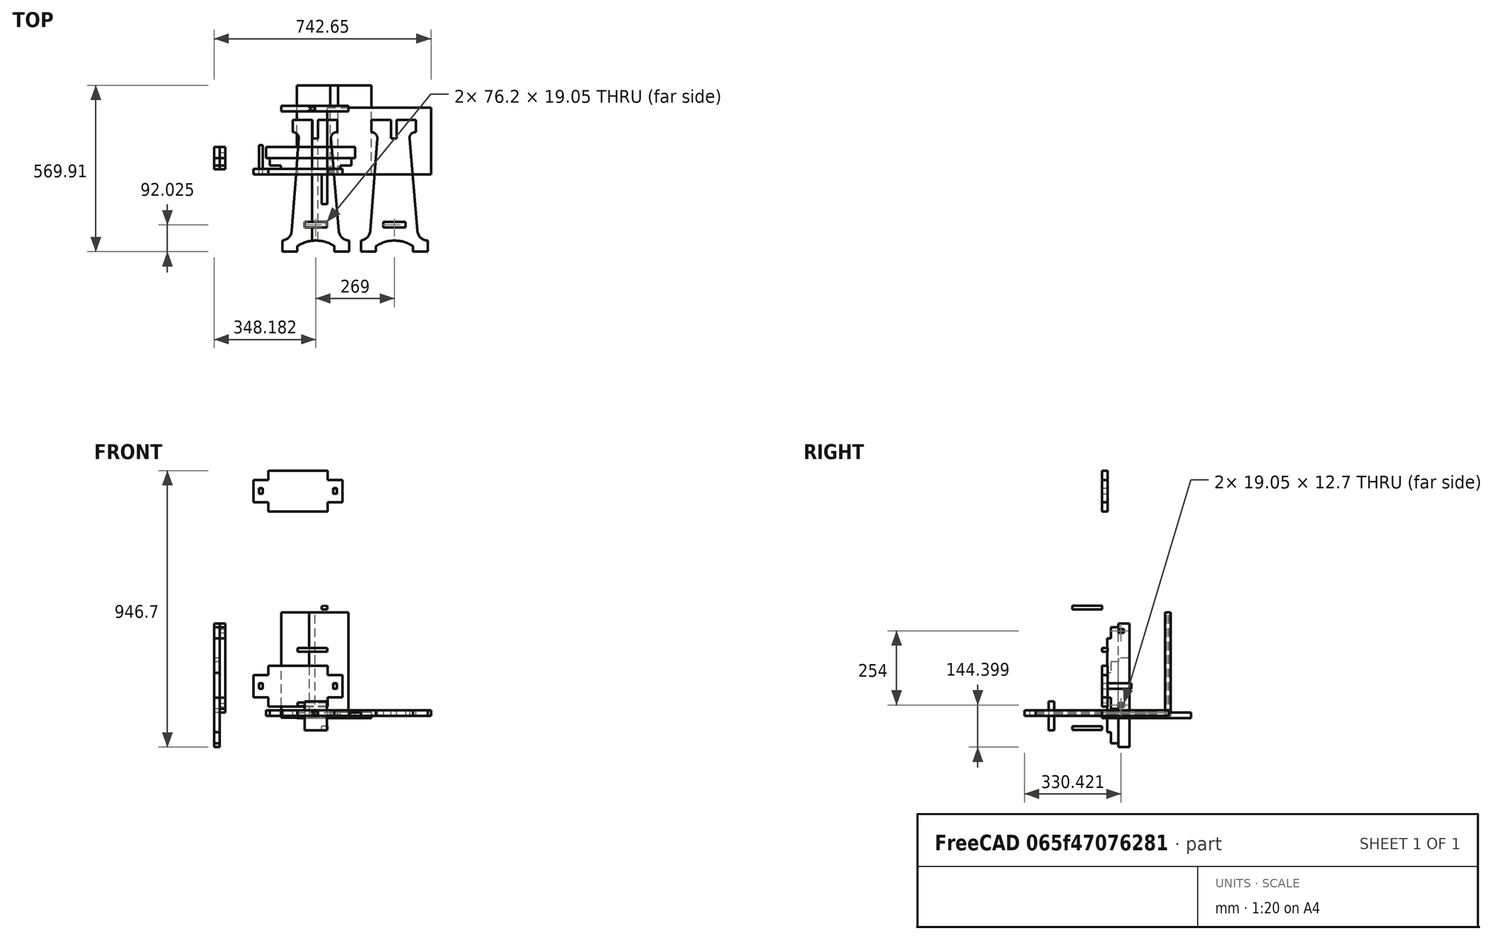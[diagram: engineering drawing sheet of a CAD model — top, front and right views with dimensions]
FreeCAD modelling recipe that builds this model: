
FCSTD DOCUMENT  (FreeCAD 0.20R29177 +426 (Git))
Label: little_table
License: All rights reserved
LicenseURL: http://en.wikipedia.org/wiki/All_rights_reserved
objects: Part::Feature×79, Sketcher::SketchObject×29, Part::Extrusion×28, App::Part×19, Surface::Filling×13, Part::Cut×8, Part::Compound×8, PartDesign::ShapeBinder×5, Part::Wedge×4, Part::Box×4, Part::Part2DObjectPython×4, Surface::GeomFillSurface×4, Part::FeaturePython×3, Part::Face×2, App::FeaturePython×2, App::DocumentObjectGroup×2, Part::MultiFuse×2, Part::Sweep×1, PartDesign::Body×1, Mesh::Feature×1
note: 195 computed .brp shape members not serialized (recipe doc carries the construction recipe); baked Part::Feature solids carry a one-line shape summary decoded from their .brp

FEATURE [Sketcher::SketchObject] Sketch001  label="side"
  FullyConstrained = false
  MapMode = 5
  sketch-geometry (21):
    g0: LineSegment StartX=-117.157 StartY=185.74 StartZ=0 EndX=-50.4825 EndY=185.74 EndZ=0
    g1: LineSegment StartX=-50.4825 StartY=185.74 StartZ=0 EndX=-50.4825 EndY=122.24 EndZ=0
    g2: LineSegment StartX=-50.4825 StartY=122.24 StartZ=0 EndX=-31.4325 EndY=122.24 EndZ=0
    g3: LineSegment StartX=-31.4325 StartY=122.24 StartZ=0 EndX=-31.4325 EndY=185.74 EndZ=0
    g4: LineSegment StartX=-31.4325 StartY=185.74 StartZ=0 EndX=35.2425 EndY=185.74 EndZ=0
    g5: LineSegment StartX=35.2425 StartY=185.74 StartZ=0 EndX=35.2425 EndY=144.465 EndZ=0
    g6: LineSegment StartX=13.0136 StartY=122.055 StartZ=0 EndX=39.774 EndY=-193.522 EndZ=0
    g7: LineSegment StartX=75.3816 StartY=-226.922 StartZ=0 EndX=75.3816 EndY=-265.022 EndZ=0
    g8: LineSegment StartX=75.3816 StartY=-265.022 StartZ=0 EndX=24.5816 EndY=-265.022 EndZ=0
    g9: LineSegment StartX=24.5816 StartY=-265.022 StartZ=0 EndX=24.5816 EndY=-245.972 EndZ=0
    g10: LineSegment StartX=-102.318 StartY=-246.06 StartZ=0 EndX=-102.318 EndY=-265.11 EndZ=0
    g11: LineSegment StartX=-153.118 StartY=-265.11 StartZ=0 EndX=-153.118 EndY=-227.01 EndZ=0
    g12: LineSegment StartX=-121.447 StartY=-193.607 StartZ=0 EndX=-97.2982 EndY=122.181 EndZ=0
    g13: LineSegment StartX=-117.157 StartY=144.465 StartZ=0 EndX=-117.157 EndY=185.74 EndZ=0
    g14: LineSegment StartX=-153.118 StartY=-265.11 StartZ=0 EndX=-102.318 EndY=-265.11 EndZ=0
    g15: ArcOfCircle CenterX=-38.802 CenterY=-341.893 CenterZ=0 NormalX=0 NormalY=0 NormalZ=1 AngleXU=0 Radius=114.971 StartAngle=0.986872 EndAngle=2.15611
    g16: LineSegment StartX=-79.2401 StartY=-226.922 StartZ=0 EndX=17.3359 EndY=-226.922 EndZ=0
    g17: ArcOfCircle CenterX=-157.831 CenterY=-190.825 CenterZ=0 NormalX=0 NormalY=0 NormalZ=1 AngleXU=0 Radius=36.4906 StartAngle=4.8419 EndAngle=6.20686
    g18: ArcOfCircle CenterX=-117.958 CenterY=123.761 CenterZ=0 NormalX=0 NormalY=0 NormalZ=1 AngleXU=0 Radius=20.7201 StartAngle=6.20686 EndAngle=7.81534
    g19: ArcOfCircle CenterX=33.6596 CenterY=123.806 CenterZ=0 NormalX=0 NormalY=0 NormalZ=1 AngleXU=0 Radius=20.7201 StartAngle=1.49433 EndAngle=3.22619
    g20: ArcOfCircle CenterX=76.1341 CenterY=-190.439 CenterZ=0 NormalX=0 NormalY=0 NormalZ=1 AngleXU=0 Radius=36.4906 StartAngle=3.22619 EndAngle=4.69177
  constraints (54):
    c: Coincident(g1,g0)
    c: Vertical(g1)
    c: Coincident(g2,g1)
    c: Coincident(g3,g2)
    c: Coincident(g4,g3)
    c: Horizontal(g4)
    c: Coincident(g5,g4)
    c: Vertical(g5)
    c: Vertical(g7)
    c: Coincident(g8,g7)
    c: Coincident(g9,g8)
    c: Coincident(g13,g0)
    c: Vertical(g13)
    c: Coincident(g14,g10)
    c: Vertical(g3)
    c: Vertical(g11)
    c: Vertical(g10)
    c: Vertical(g9)
    c: Horizontal(g8)
    c: Horizontal(g14)
    c: Horizontal(g0)
    c: Horizontal(g2)
    c: Equal(g4,g0)
    c: Equal(g12,g6)
    c: Equal(g5,g13)
    c: Equal(g11,g7)
    c: Coincident(g11,g14)
    c: Equal(g14,g8)
    c: Equal(g10,g9)
    c: Equal(g3,g1)
    c: DistanceY(g7,g7) = 38.1
    c: DistanceX(g14,g14) = 50.8
    c: DistanceX(g11,g7) = 228.5
    c: DistanceY(g11,g0) = 450.85
    c: DistanceY(g10,g10) = 19.05
    c: DistanceY(g1,g1) = 63.5
    c: DistanceX(g2,g2) = 19.05
    c: DistanceX(g0,g4) = 152.4
    c: DistanceY(g13,g13) = 41.275
    c: Coincident(g15,g9)
    c: Horizontal(g16)
    c: Tangent(g16,g15)
    c: DistanceY(g7,g16) = 38.1
    c: Coincident(g15,g10)
    c: Coincident(g17,g11)
    c: Coincident(g19,g5)
    c: Tangent(g18,g12) = -1.5708
    c: Tangent(g17,g12) = -1.5708
    c: Tangent(g20,g6) = -1.5708
    c: Equal(g19,g18)
    c: Equal(g17,g20)
    c: Coincident(g18,g13)
    c: Tangent(g19,g6) = -1.5708
    c: Coincident(g20,g7)
FEATURE [Part::FeaturePython] Connect  # WARN: FeaturePython — macro-defined, semantics opaque (R4)
  Objects = -> [Sketch001]
  Tolerance = 0
FEATURE [Part::Extrusion] Extrude
  Base = -> Connect
  Dir = (0,0,1)
  DirMode = 2
  FaceMakerClass = Part::FaceMakerBullseye
  LengthFwd = 19.05
  LengthRev = 0
  Solid = true
  Symmetric = false
FEATURE [Part::Extrusion] Extrude001  label="solid_side_leg"
  Base = -> Connect
  Dir = (0,0,1)
  DirMode = 2
  FaceMakerClass = Part::FaceMakerBullseye
  LengthFwd = 19.05
  LengthRev = 0
  Solid = true
  Symmetric = false
FEATURE [Sketcher::SketchObject] Sketch002  label="side_hole"
  ExternalGeometry = -> [Sketch001]
  FullyConstrained = true
  MapMode = 5
  sketch-geometry (4):
    g0: LineSegment StartX=-76.9684 StartY=-163.56 StartZ=0 EndX=-0.768384 EndY=-163.56 EndZ=0
    g1: LineSegment StartX=-0.768384 StartY=-163.56 StartZ=0 EndX=-0.768384 EndY=-182.61 EndZ=0
    g2: LineSegment StartX=-0.768384 StartY=-182.61 StartZ=0 EndX=-76.9684 EndY=-182.61 EndZ=0
    g3: LineSegment StartX=-76.9684 StartY=-182.61 StartZ=0 EndX=-76.9684 EndY=-163.56 EndZ=0
  constraints (12):
    c: Horizontal(g0)
    c: Coincident(g1,g0)
    c: Coincident(g2,g1)
    c: Horizontal(g2)
    c: Vertical(g3)
    c: Coincident(g0,g3)
    c: Coincident(g3,g2)
    c: Vertical(g1)
    c: DistanceX(g0,g0) = 76.2
    c: DistanceY(g3,g3) = 19.05
    c: DistanceY(g-3,g2) = 82.5
    c: DistanceX(g-4,g2) = 76.15
FEATURE [Part::Face] Face
  FaceMakerClass = Part::FaceMakerBullseye
  Sources = -> [Sketch002]
FEATURE [Part::Extrusion] Extrude002  label="rectangular_hole"
  Base = -> Face
  Dir = (0,0,-1)
  DirMode = 0
  FaceMakerClass = Part::FaceMakerBullseye
  LengthFwd = 100
  LengthRev = 0
  Solid = true
  Symmetric = true
FEATURE [PartDesign::ShapeBinder] ShapeBinder
  Support = -> [Extrude001]
  TraceSupport = false
FEATURE [PartDesign::ShapeBinder] ShapeBinder001
  Support = -> [Extrude002]
  TraceSupport = false
FEATURE [Part::Cut] Cut  label="Finished_Side_Leg"
  Base = -> ShapeBinder
  Tool = -> ShapeBinder001
FEATURE [Sketcher::SketchObject] Sketch003  label="hole1"
  FullyConstrained = true
  MapMode = 5
  Placement = pos=(0,0,0) rot=(0.57735,0.57735,0.57735;2.0944rad)
  Support = -> [YZ_Plane007]
FEATURE [Sketcher::SketchObject] Sketch004  label="side001"
  FullyConstrained = false
  MapMode = 5
  Support = -> [XY_Plane006]
  sketch-geometry (21):
    g0: LineSegment StartX=-117.157 StartY=185.74 StartZ=0 EndX=-50.4825 EndY=185.74 EndZ=0
    g1: LineSegment StartX=-50.4825 StartY=185.74 StartZ=0 EndX=-50.4825 EndY=122.24 EndZ=0
    g2: LineSegment StartX=-50.4825 StartY=122.24 StartZ=0 EndX=-31.4325 EndY=122.24 EndZ=0
    g3: LineSegment StartX=-31.4325 StartY=122.24 StartZ=0 EndX=-31.4325 EndY=185.74 EndZ=0
    g4: LineSegment StartX=-31.4325 StartY=185.74 StartZ=0 EndX=35.2425 EndY=185.74 EndZ=0
    g5: LineSegment StartX=35.2425 StartY=185.74 StartZ=0 EndX=35.2425 EndY=144.465 EndZ=0
    g6: LineSegment StartX=13.0136 StartY=122.055 StartZ=0 EndX=39.774 EndY=-193.522 EndZ=0
    g7: LineSegment StartX=75.3816 StartY=-226.922 StartZ=0 EndX=75.3816 EndY=-265.022 EndZ=0
    g8: LineSegment StartX=75.3816 StartY=-265.022 StartZ=0 EndX=24.5816 EndY=-265.022 EndZ=0
    g9: LineSegment StartX=24.5816 StartY=-265.022 StartZ=0 EndX=24.5816 EndY=-245.972 EndZ=0
    g10: LineSegment StartX=-102.318 StartY=-246.06 StartZ=0 EndX=-102.318 EndY=-265.11 EndZ=0
    g11: LineSegment StartX=-153.118 StartY=-265.11 StartZ=0 EndX=-153.118 EndY=-227.01 EndZ=0
    g12: LineSegment StartX=-121.447 StartY=-193.607 StartZ=0 EndX=-97.2982 EndY=122.181 EndZ=0
    g13: LineSegment StartX=-117.157 StartY=144.465 StartZ=0 EndX=-117.157 EndY=185.74 EndZ=0
    g14: LineSegment StartX=-153.118 StartY=-265.11 StartZ=0 EndX=-102.318 EndY=-265.11 EndZ=0
    g15: ArcOfCircle CenterX=-38.802 CenterY=-341.893 CenterZ=0 NormalX=0 NormalY=0 NormalZ=1 AngleXU=0 Radius=114.971 StartAngle=0.986872 EndAngle=2.15611
    g16: LineSegment StartX=-79.2401 StartY=-226.922 StartZ=0 EndX=17.3359 EndY=-226.922 EndZ=0
    g17: ArcOfCircle CenterX=-157.831 CenterY=-190.825 CenterZ=0 NormalX=0 NormalY=0 NormalZ=1 AngleXU=0 Radius=36.4906 StartAngle=4.8419 EndAngle=6.20686
    g18: ArcOfCircle CenterX=-117.958 CenterY=123.761 CenterZ=0 NormalX=0 NormalY=0 NormalZ=1 AngleXU=0 Radius=20.7201 StartAngle=6.20686 EndAngle=7.81534
    g19: ArcOfCircle CenterX=33.6596 CenterY=123.806 CenterZ=0 NormalX=0 NormalY=0 NormalZ=1 AngleXU=0 Radius=20.7201 StartAngle=1.49433 EndAngle=3.22619
    g20: ArcOfCircle CenterX=76.1341 CenterY=-190.439 CenterZ=0 NormalX=0 NormalY=0 NormalZ=1 AngleXU=0 Radius=36.4906 StartAngle=3.22619 EndAngle=4.69177
  constraints (54):
    c: Coincident(g1,g0)
    c: Vertical(g1)
    c: Coincident(g2,g1)
    c: Coincident(g3,g2)
    c: Coincident(g4,g3)
    c: Horizontal(g4)
    c: Coincident(g5,g4)
    c: Vertical(g5)
    c: Vertical(g7)
    c: Coincident(g8,g7)
    c: Coincident(g9,g8)
    c: Coincident(g13,g0)
    c: Vertical(g13)
    c: Coincident(g14,g10)
    c: Vertical(g3)
    c: Vertical(g11)
    c: Vertical(g10)
    c: Vertical(g9)
    c: Horizontal(g8)
    c: Horizontal(g14)
    c: Horizontal(g0)
    c: Horizontal(g2)
    c: Equal(g4,g0)
    c: Equal(g12,g6)
    c: Equal(g5,g13)
    c: Equal(g11,g7)
    c: Coincident(g11,g14)
    c: Equal(g14,g8)
    c: Equal(g10,g9)
    c: Equal(g3,g1)
    c: DistanceY(g7,g7) = 38.1
    c: DistanceX(g14,g14) = 50.8
    c: DistanceX(g11,g7) = 228.5
    c: DistanceY(g11,g0) = 450.85
    c: DistanceY(g10,g10) = 19.05
    c: DistanceY(g1,g1) = 63.5
    c: DistanceX(g2,g2) = 19.05
    c: DistanceX(g0,g4) = 152.4
    c: DistanceY(g13,g13) = 41.275
    c: Coincident(g15,g9)
    c: Horizontal(g16)
    c: Tangent(g16,g15)
    c: DistanceY(g7,g16) = 38.1
    c: Coincident(g15,g10)
    c: Coincident(g17,g11)
    c: Coincident(g19,g5)
    c: Tangent(g18,g12) = -1.5708
    c: Tangent(g17,g12) = -1.5708
    c: Tangent(g20,g6) = -1.5708
    c: Equal(g19,g18)
    c: Equal(g17,g20)
    c: Coincident(g18,g13)
    c: Tangent(g19,g6) = -1.5708
    c: Coincident(g20,g7)
FEATURE [Part::FeaturePython] Connect001  # WARN: FeaturePython — macro-defined, semantics opaque (R4)
  Objects = -> [Sketch004]
  Tolerance = 0
FEATURE [Part::Extrusion] Extrude003
  Base = -> Connect001
  Dir = (0,0,1)
  DirMode = 2
  FaceMakerClass = Part::FaceMakerBullseye
  LengthFwd = 19.05
  LengthRev = 0
  Solid = true
  Symmetric = false
FEATURE [Part::Extrusion] Extrude004  label="solid_side_leg001"
  Base = -> Connect001
  Dir = (0,0,1)
  DirMode = 2
  FaceMakerClass = Part::FaceMakerBullseye
  LengthFwd = 19.05
  LengthRev = 0
  Solid = true
  Symmetric = false
FEATURE [PartDesign::ShapeBinder] ShapeBinder002
  Support = -> [Extrude004]
  TraceSupport = false
FEATURE [Sketcher::SketchObject] Sketch005  label="side_hole001"
  ExternalGeometry = -> [Sketch004]
  FullyConstrained = true
  MapMode = 5
  Support = -> [XY_Plane006]
  sketch-geometry (4):
    g0: LineSegment StartX=-76.9684 StartY=-163.56 StartZ=0 EndX=-0.768384 EndY=-163.56 EndZ=0
    g1: LineSegment StartX=-0.768384 StartY=-163.56 StartZ=0 EndX=-0.768384 EndY=-182.61 EndZ=0
    g2: LineSegment StartX=-0.768384 StartY=-182.61 StartZ=0 EndX=-76.9684 EndY=-182.61 EndZ=0
    g3: LineSegment StartX=-76.9684 StartY=-182.61 StartZ=0 EndX=-76.9684 EndY=-163.56 EndZ=0
  constraints (12):
    c: Horizontal(g0)
    c: Coincident(g1,g0)
    c: Coincident(g2,g1)
    c: Horizontal(g2)
    c: Vertical(g3)
    c: Coincident(g0,g3)
    c: Coincident(g3,g2)
    c: Vertical(g1)
    c: DistanceX(g0,g0) = 76.2
    c: DistanceY(g3,g3) = 19.05
    c: DistanceY(g-3,g2) = 82.5
    c: DistanceX(g-4,g2) = 76.15
FEATURE [Part::Face] Face001
  FaceMakerClass = Part::FaceMakerBullseye
  Sources = -> [Sketch005]
FEATURE [Part::Extrusion] Extrude005  label="rectangular_hole001"
  Base = -> Face001
  Dir = (0,0,-1)
  DirMode = 0
  FaceMakerClass = Part::FaceMakerBullseye
  LengthFwd = 100
  LengthRev = 0
  Solid = true
  Symmetric = true
FEATURE [PartDesign::ShapeBinder] ShapeBinder003
  Support = -> [Extrude005]
  TraceSupport = false
FEATURE [Part::Cut] Cut001  label="Finished_Side_Leg001"
  Base = -> ShapeBinder002
  Placement = pos=(269,0,0) rot=(0,0,1;0rad)
  Tool = -> ShapeBinder003
FEATURE [Sketcher::SketchObject] Sketch006  label="shelf"
  FullyConstrained = false
  MapMode = 5
  Placement = pos=(0,0,0) rot=(1,0,0;1.5708rad)
  Support = -> [XZ_Plane007]
  sketch-geometry (19):
    g0: LineSegment StartX=-202.002 StartY=139.919 StartZ=0 EndX=-202.002 EndY=63.7195 EndZ=0
    g1: LineSegment StartX=-202.002 StartY=63.7195 StartZ=0 EndX=-252.802 EndY=63.7195 EndZ=0
    g2: LineSegment StartX=-252.802 StartY=63.7195 StartZ=0 EndX=-252.802 EndY=139.919 EndZ=0
    g3: LineSegment StartX=-252.802 StartY=139.919 StartZ=0 EndX=-202.002 EndY=139.919 EndZ=0
    g4: LineSegment StartX=-202.002 StartY=139.919 StartZ=0 EndX=-202.002 EndY=171.669 EndZ=0
    g5: LineSegment StartX=-202.002 StartY=63.7195 StartZ=0 EndX=-202.002 EndY=31.9695 EndZ=0
    g6: LineSegment StartX=1.18793 StartY=171.669 StartZ=0 EndX=1.18793 EndY=139.919 EndZ=0
    g7: LineSegment StartX=1.18793 StartY=139.919 StartZ=0 EndX=51.9879 EndY=139.919 EndZ=0
    g8: LineSegment StartX=51.9879 StartY=139.919 StartZ=0 EndX=51.9879 EndY=63.7195 EndZ=0
    g9: LineSegment StartX=51.9879 StartY=63.7195 StartZ=0 EndX=1.18793 EndY=63.7195 EndZ=0
    g10: LineSegment StartX=1.18793 StartY=63.7195 StartZ=0 EndX=1.18793 EndY=31.9695 EndZ=0
    g11: LineSegment StartX=-202.002 StartY=171.669 StartZ=0 EndX=1.18793 EndY=171.669 EndZ=0
    g12: LineSegment StartX=-202.002 StartY=31.9695 StartZ=0 EndX=1.18793 EndY=31.9695 EndZ=0
    g13: LineSegment StartX=1.18793 StartY=139.919 StartZ=0 EndX=1.18793 EndY=63.7195 EndZ=0
    g14: LineSegment StartX=-221.052 StartY=139.919 StartZ=0 EndX=-221.052 EndY=63.7195 EndZ=0
    g15: LineSegment StartX=20.2379 StartY=139.919 StartZ=0 EndX=20.2379 EndY=63.7195 EndZ=0
    g16: LineSegment StartX=20.2379 StartY=63.7195 StartZ=0 EndX=0.408682 EndY=63.7195 EndZ=0
    g17: LineSegment StartX=51.9879 StartY=63.7195 StartZ=0 EndX=20.2379 EndY=63.7195 EndZ=0
    g18: LineSegment StartX=-221.052 StartY=63.7195 StartZ=0 EndX=-252.802 EndY=63.7195 EndZ=0
  constraints (51):
    c: Vertical(g0)
    c: Coincident(g1,g0)
    c: Horizontal(g1)
    c: Coincident(g2,g1)
    c: Vertical(g2)
    c: Coincident(g3,g2)
    c: Coincident(g3,g0)
    c: Horizontal(g3)
    c: Distance(g2) = 76.2
    c: Distance(g3) = 50.8
    c: Perpendicular(g3,g4)
    c: Coincident(g4,g0)
    c: Coincident(g5,g0)
    c: Vertical(g5)
    c: Equal(g5,g4)
    c: Vertical(g6)
    c: Coincident(g7,g6)
    c: Horizontal(g7)
    c: Coincident(g8,g7)
    c: Vertical(g8)
    c: Coincident(g9,g8)
    c: Horizontal(g9)
    c: Coincident(g10,g9)
    c: Vertical(g10)
    c: Distance(g2,g7) = 304.79
    c: Coincident(g11,g4)
    c: Coincident(g11,g6)
    c: Horizontal(g11)
    c: Coincident(g12,g5)
    c: Coincident(g12,g10)
    c: Horizontal(g12)
    c: Equal(g6,g10)
    c: Equal(g10,g5)
    c: Equal(g3,g7)
    c: Equal(g7,g9)
    c: Coincident(g13,g6)
    c: Coincident(g13,g9)
    c: PointOnObject(g14,g3)
    c: PointOnObject(g14,g1)
    c: Vertical(g14)
    c: PointOnObject(g15,g7)
    c: PointOnObject(g15,g9)
    c: Vertical(g15)
    c: Distance(g14,g1) = 31.75
    c: Coincident(g16,g15)
    c: Coincident(g17,g8)
    c: Coincident(g17,g15)
    c: Coincident(g18,g14)
    c: Coincident(g18,g1)
    c: Equal(g17,g18)
    c: Distance(g6,g10) = 139.7
FEATURE [Surface::Filling] Surface
  Anisotropy = false
  BoundaryEdges = -> [Sketch006]
  BoundaryOrder = [0,0,0,0,0,0,0,0,0,0,0,0]
  Degree = 3
  Iterations = 2
  MaximumDegree = 8
  MaximumSegments = 9
  PointsOnCurve = 15
  TolAngular = 0.01
  TolCurvature = 0.1
  Tolerance2d = 1e-05
  Tolerance3d = 0.0001
FEATURE [Part::Extrusion] Extrude006
  Base = -> Surface
  Dir = (0,19.05,0)
  DirMode = 0
  FaceMakerClass = Part::FaceMakerBullseye
  LengthFwd = 19.05
  LengthRev = 0
  Solid = true
  Symmetric = false
FEATURE [Sketcher::SketchObject] Sketch008  label="shelf001"
  FullyConstrained = false
  MapMode = 5
  Placement = pos=(0,0,0) rot=(1,0,0;1.5708rad)
  Support = -> [XZ_Plane008]
  sketch-geometry (19):
    g0: LineSegment StartX=-202.002 StartY=139.919 StartZ=0 EndX=-202.002 EndY=63.7195 EndZ=0
    g1: LineSegment StartX=-202.002 StartY=63.7195 StartZ=0 EndX=-252.802 EndY=63.7195 EndZ=0
    g2: LineSegment StartX=-252.802 StartY=63.7195 StartZ=0 EndX=-252.802 EndY=139.919 EndZ=0
    g3: LineSegment StartX=-252.802 StartY=139.919 StartZ=0 EndX=-202.002 EndY=139.919 EndZ=0
    g4: LineSegment StartX=-202.002 StartY=139.919 StartZ=0 EndX=-202.002 EndY=171.669 EndZ=0
    g5: LineSegment StartX=-202.002 StartY=63.7195 StartZ=0 EndX=-202.002 EndY=31.9695 EndZ=0
    g6: LineSegment StartX=1.18793 StartY=171.669 StartZ=0 EndX=1.18793 EndY=139.919 EndZ=0
    g7: LineSegment StartX=1.18793 StartY=139.919 StartZ=0 EndX=51.9879 EndY=139.919 EndZ=0
    g8: LineSegment StartX=51.9879 StartY=139.919 StartZ=0 EndX=51.9879 EndY=63.7195 EndZ=0
    g9: LineSegment StartX=51.9879 StartY=63.7195 StartZ=0 EndX=1.18793 EndY=63.7195 EndZ=0
    g10: LineSegment StartX=1.18793 StartY=63.7195 StartZ=0 EndX=1.18793 EndY=31.9695 EndZ=0
    g11: LineSegment StartX=-202.002 StartY=171.669 StartZ=0 EndX=1.18793 EndY=171.669 EndZ=0
    g12: LineSegment StartX=-202.002 StartY=31.9695 StartZ=0 EndX=1.18793 EndY=31.9695 EndZ=0
    g13: LineSegment StartX=1.18793 StartY=139.919 StartZ=0 EndX=1.18793 EndY=63.7195 EndZ=0
    g14: LineSegment StartX=-221.052 StartY=139.919 StartZ=0 EndX=-221.052 EndY=63.7195 EndZ=0
    g15: LineSegment StartX=20.2379 StartY=139.919 StartZ=0 EndX=20.2379 EndY=63.7195 EndZ=0
    g16: LineSegment StartX=20.2379 StartY=63.7195 StartZ=0 EndX=0.408682 EndY=63.7195 EndZ=0
    g17: LineSegment StartX=51.9879 StartY=63.7195 StartZ=0 EndX=20.2379 EndY=63.7195 EndZ=0
    g18: LineSegment StartX=-221.052 StartY=63.7195 StartZ=0 EndX=-252.802 EndY=63.7195 EndZ=0
  constraints (51):
    c: Vertical(g0)
    c: Coincident(g1,g0)
    c: Horizontal(g1)
    c: Coincident(g2,g1)
    c: Vertical(g2)
    c: Coincident(g3,g2)
    c: Coincident(g3,g0)
    c: Horizontal(g3)
    c: Distance(g2) = 76.2
    c: Distance(g3) = 50.8
    c: Perpendicular(g3,g4)
    c: Coincident(g4,g0)
    c: Coincident(g5,g0)
    c: Vertical(g5)
    c: Equal(g5,g4)
    c: Vertical(g6)
    c: Coincident(g7,g6)
    c: Horizontal(g7)
    c: Coincident(g8,g7)
    c: Vertical(g8)
    c: Coincident(g9,g8)
    c: Horizontal(g9)
    c: Coincident(g10,g9)
    c: Vertical(g10)
    c: Distance(g2,g7) = 304.79
    c: Coincident(g11,g4)
    c: Coincident(g11,g6)
    c: Horizontal(g11)
    c: Coincident(g12,g5)
    c: Coincident(g12,g10)
    c: Horizontal(g12)
    c: Equal(g6,g10)
    c: Equal(g10,g5)
    c: Equal(g3,g7)
    c: Equal(g7,g9)
    c: Coincident(g13,g6)
    c: Coincident(g13,g9)
    c: PointOnObject(g14,g3)
    c: PointOnObject(g14,g1)
    c: Vertical(g14)
    c: PointOnObject(g15,g7)
    c: PointOnObject(g15,g9)
    c: Vertical(g15)
    c: Distance(g14,g1) = 31.75
    c: Coincident(g16,g15)
    c: Coincident(g17,g8)
    c: Coincident(g17,g15)
    c: Coincident(g18,g14)
    c: Coincident(g18,g1)
    c: Equal(g17,g18)
    c: Distance(g6,g10) = 139.7
FEATURE [Sketcher::SketchObject] Sketch009
  ExternalGeometry = -> [Sketch008]
  FullyConstrained = true
  Placement = pos=(0,0,0) rot=(1,0,0;1.5708rad)
  sketch-geometry (4):
    g0: LineSegment StartX=-221.052 StartY=111.344 StartZ=0 EndX=-233.752 EndY=111.344 EndZ=0
    g1: LineSegment StartX=-233.752 StartY=111.344 StartZ=0 EndX=-233.752 EndY=92.2945 EndZ=0
    g2: LineSegment StartX=-233.752 StartY=92.2945 StartZ=0 EndX=-221.052 EndY=92.2945 EndZ=0
    g3: LineSegment StartX=-221.052 StartY=92.2945 StartZ=0 EndX=-221.052 EndY=111.344 EndZ=0
  constraints (12):
    c: Coincident(g0,g1)
    c: Coincident(g1,g2)
    c: Coincident(g2,g3)
    c: Coincident(g3,g0)
    c: Horizontal(g0)
    c: Horizontal(g2)
    c: Vertical(g1)
    c: Vertical(g3)
    c: Distance(g3) = 19.05
    c: Distance(g0) = 12.7
    c: PointOnObject(g0,g-3)
    c: Distance(g0,g-3) = 28.575
FEATURE [Sketcher::SketchObject] Sketch010
  ExternalGeometry = -> [Sketch006]
  FullyConstrained = true
  MapMode = 2
  Placement = pos=(0,0,0) rot=(1,0,0;1.5708rad)
  Support = -> [Sketch006]
  sketch-geometry (4):
    g0: LineSegment StartX=20.2379 StartY=111.344 StartZ=0 EndX=32.9379 EndY=111.344 EndZ=0
    g1: LineSegment StartX=32.9379 StartY=111.344 StartZ=0 EndX=32.9379 EndY=92.2945 EndZ=0
    g2: LineSegment StartX=32.9379 StartY=92.2945 StartZ=0 EndX=20.2379 EndY=92.2945 EndZ=0
    g3: LineSegment StartX=20.2379 StartY=92.2945 StartZ=0 EndX=20.2379 EndY=111.344 EndZ=0
  constraints (12):
    c: Coincident(g0,g1)
    c: Coincident(g1,g2)
    c: Coincident(g2,g3)
    c: Coincident(g3,g0)
    c: Horizontal(g0)
    c: Horizontal(g2)
    c: Vertical(g1)
    c: Vertical(g3)
    c: Distance(g1) = 19.05
    c: Distance(g0) = 12.7
    c: PointOnObject(g0,g-3)
    c: Distance(g0,g-3) = 28.575
FEATURE [Surface::Filling] Surface007  label="hole2"
  Anisotropy = false
  BoundaryEdges = -> [Sketch010]
  BoundaryOrder = [0,0,0,0]
  Degree = 3
  Iterations = 2
  MaximumDegree = 8
  MaximumSegments = 9
  PointsOnCurve = 15
  TolAngular = 0.01
  TolCurvature = 0.1
  Tolerance2d = 1e-05
  Tolerance3d = 0.0001
FEATURE [Surface::Filling] Surface008  label="hole003"
  Anisotropy = false
  BoundaryEdges = -> [Sketch009]
  BoundaryOrder = [0,0,0,0]
  Degree = 3
  Iterations = 2
  MaximumDegree = 8
  MaximumSegments = 9
  PointsOnCurve = 15
  TolAngular = 0.01
  TolCurvature = 0.1
  Tolerance2d = 1e-05
  Tolerance3d = 0.0001
FEATURE [Part::Extrusion] Extrude007
  Base = -> Surface008
  Dir = (0,200,0)
  DirMode = 0
  FaceMakerClass = Part::FaceMakerBullseye
  LengthFwd = 100
  LengthRev = 0
  Solid = true
  Symmetric = false
FEATURE [Part::Extrusion] Extrude008
  Base = -> Surface008
  Dir = (0,100,0)
  DirMode = 0
  FaceMakerClass = Part::FaceMakerBullseye
  LengthFwd = 100
  LengthRev = 0
  Solid = true
  Symmetric = false
FEATURE [Part::Cut] Cut002
  Base = -> Extrude006
  Tool = -> Extrude007
FEATURE [Part::Extrusion] Extrude009
  Base = -> Surface007
  Dir = (0,100,-1)
  DirMode = 0
  FaceMakerClass = Part::FaceMakerBullseye
  LengthFwd = 100
  LengthRev = 0
  Solid = false
  Symmetric = false
FEATURE [Part::Cut] Cut003
  Base = -> Cut002
  Tool = -> Extrude009
FEATURE [Sketcher::SketchObject] Sketch011
  FullyConstrained = false
  MapMode = 5
  Placement = pos=(0,0,0) rot=(0.57735,0.57735,0.57735;2.0944rad)
  Support = -> [YZ_Plane014]
  sketch-geometry (4):
    g0: LineSegment StartX=-13 StartY=37.953 StartZ=0 EndX=0 EndY=37.953 EndZ=0
    g1: LineSegment StartX=0 StartY=37.953 StartZ=0 EndX=0 EndY=18.903 EndZ=0
    g2: LineSegment StartX=0 StartY=18.903 StartZ=0 EndX=-13 EndY=18.903 EndZ=0
    g3: LineSegment StartX=-13 StartY=18.903 StartZ=0 EndX=-13 EndY=37.953 EndZ=0
  constraints (11):
    c: Coincident(g0,g1)
    c: Coincident(g1,g2)
    c: Coincident(g2,g3)
    c: Coincident(g3,g0)
    c: Horizontal(g0)
    c: Horizontal(g2)
    c: Vertical(g1)
    c: Vertical(g3)
    c: PointOnObject(g1,g-2)
    c: Distance(g0) = 13
    c: Distance(g1) = 19.05
FEATURE [App::Part] Part007
  Origin = -> Origin009
FEATURE [App::Part] Part
  Group = -> [Part007]
  Origin = -> Origin008
FEATURE [Part::Wedge] Wedge
  AttacherType = Attacher::AttachEngine3D
  Placement = pos=(0,4.4e-14,364) rot=(0.57735,-0.57735,0.57735;2.0944rad)
  X2max = 12
  X2min = 0
  Xmax = 13
  Xmin = 0
  Ymax = 19.05
  Ymin = 0
  Z2max = 101.6
  Z2min = 0
  Zmax = 101.6
  Zmin = 0
FEATURE [Part::Wedge] Wedge001
  AttacherType = Attacher::AttachEngine3D
  Placement = pos=(0,4.4e-14,-48) rot=(0.57735,-0.57735,0.57735;2.0944rad)
  X2max = 12
  X2min = 0
  Xmax = 13
  Xmin = 0
  Ymax = 19.05
  Ymin = 0
  Z2max = 101.6
  Z2min = 0
  Zmax = 101.6
  Zmin = 0
FEATURE [Part::Wedge] Wedge002
  AttacherType = Attacher::AttachEngine3D
  Placement = pos=(-1.6e-14,4.4e-14,220) rot=(0,-1,0;1.5708rad)
  X2max = 12
  X2min = 0
  Xmax = 13
  Xmin = 0
  Ymax = 19.05
  Ymin = 0
  Z2max = 101.6
  Z2min = 0
  Zmax = 101.6
  Zmin = 0
FEATURE [Part::Wedge] Wedge003
  AttacherType = Attacher::AttachEngine3D
  Placement = pos=(-1.8e-14,4.4e-14,33) rot=(0,-1,0;1.5708rad)
  X2max = 12
  X2min = 0
  Xmax = 13
  Xmin = 0
  Ymax = 19.05
  Ymin = 0
  Z2max = 101.6
  Z2min = 0
  Zmax = 101.6
  Zmin = 0
FEATURE [App::Part] Part008  label="wedge"
  Group = -> [Wedge,Wedge001,Wedge002,Wedge003]
  Origin = -> Origin010
FEATURE [Part::Box] Box
  AttacherType = Attacher::AttachEngine3D
  Height = 19
  Length = 360
  Placement = pos=(-157,216,-6) rot=(0.57735,0.57735,0.57735;4.18879rad)
  Width = 230
FEATURE [Sketcher::SketchObject] Sketch013
  FullyConstrained = false
  MapMode = 2
  sketch-geometry (17):
    g0: LineSegment StartX=-121.471 StartY=102.917 StartZ=0 EndX=183.329 EndY=102.917 EndZ=0
    g1: ArcOfCircle CenterX=26.5868 CenterY=-67.4245 CenterZ=0 NormalX=0 NormalY=0 NormalZ=1 AngleXU=0 Radius=83.7769 StartAngle=1.18434 EndAngle=2.04007
    g2: LineSegment StartX=58.1627 StartY=10.1739 StartZ=0 EndX=110.81 EndY=10.1739 EndZ=0
    g3: LineSegment StartX=110.81 StartY=36.9335 StartZ=0 EndX=110.81 EndY=10.1739 EndZ=0
    g4: LineSegment StartX=-11.3006 StartY=7.29566 StartZ=0 EndX=-63.9482 EndY=7.29566 EndZ=0
    g5: LineSegment StartX=-63.9482 StartY=7.29566 StartZ=0 EndX=-63.9482 EndY=34.0552 EndZ=0
    g6: LineSegment StartX=-99.4978 StartY=42.1194 StartZ=0 EndX=-63.9482 EndY=34.0552 EndZ=0
    g7: LineSegment StartX=147.263 StartY=36.9335 StartZ=0 EndX=110.81 EndY=36.9335 EndZ=0
    g8: ArcOfCircle CenterX=-121.241 CenterY=53.2491 CenterZ=0 NormalX=0 NormalY=0 NormalZ=1 AngleXU=0 Radius=21.7431 StartAngle=3e-16 EndAngle=0.865607
    g9: LineSegment StartX=183.329 StartY=102.917 StartZ=0 EndX=183.329 EndY=69.8062 EndZ=0
    g10: LineSegment StartX=-121.471 StartY=102.917 StartZ=0 EndX=-121.471 EndY=69.8062 EndZ=0
    g11: LineSegment StartX=147.263 StartY=48.0632 StartZ=0 EndX=147.263 EndY=36.9335 EndZ=0
    g12: LineSegment StartX=-99.4978 StartY=53.2491 StartZ=0 EndX=-99.4978 EndY=42.1194 EndZ=0
    g13: LineSegment StartX=169.006 StartY=69.8062 StartZ=0 EndX=183.329 EndY=69.8062 EndZ=0
    g14: LineSegment StartX=-107.148 StartY=69.8062 StartZ=0 EndX=-121.471 EndY=69.8062 EndZ=0
    g15: LineSegment StartX=-107.148 StartY=69.8062 StartZ=0 EndX=169.006 EndY=69.8062 EndZ=0
    g16: ArcOfCircle CenterX=169.006 CenterY=48.0632 CenterZ=0 NormalX=0 NormalY=0 NormalZ=1 AngleXU=0 Radius=21.7431 StartAngle=1.5708 EndAngle=3.14159
  constraints (40):
    c: Horizontal(g0)
    c: Distance(g0) = 304.8
    c: Horizontal(g4)
    c: Horizontal(g7)
    c: Equal(g5,g3)
    c: Equal(g4,g2)
    c: Perpendicular(g3,g2)
    c: Coincident(g15,g8)
    c: Horizontal(g15)
    c: Coincident(g10,g14)
    c: Coincident(g9,g0)
    c: Coincident(g9,g13)
    c: Perpendicular(g0,g9)
    c: Coincident(g0,g10)
    c: Equal(g14,g13)
    c: Perpendicular(g0,g10)
    c: Coincident(g8,g14)
    c: Equal(g9,g10)
    c: Tangent(g16,g13) = 1.5708
    c: Perpendicular(g9,g13)
    c: Tangent(g16,g11) = -1.5708
    c: Coincident(g15,g13)
    c: Tangent(g8,g12) = 1.5708
    c: Coincident(g6,g12)
    c: Equal(g6,g7)
    c: Perpendicular(g0,g5)
    c: Coincident(g8,g12)
    c: Coincident(g4,g1)
    c: Coincident(g4,g5)
    c: Coincident(g16,g11)
    c: Coincident(g11,g7)
    c: Perpendicular(g0,g12)
    c: Coincident(g2,g1)
    c: Coincident(g3,g2)
    c: Coincident(g7,g3)
    c: Perpendicular(g7,g3)
    c: Equal(g16,g8)
    c: Equal(g12,g11)
    c: Perpendicular(g7,g11)
    c: Coincident(g6,g5)
FEATURE [App::FeaturePython] logo  # WARN: FeaturePython — macro-defined, semantics opaque (R4)
  BaseHeight = 0.5
  LayerHeight = 0.1
  MaximumHeight = 3
  NozzleSize = 0.4
  Path = <userpath>/Documents/glas/website/logo.png
  UpdateNotifier = 6
  ppi = 300
FEATURE [Part::Feature] Extrude010_solid  label="Extrude010 (Solid)"
  Placement = pos=(0,0,119) rot=(0,0,1;0rad)
  shape: bbox 19.05 x 80.33 x 335.3 mm, 17 faces (baked)
FEATURE [Part::FeaturePython] CrossPiece  # WARN: FeaturePython — macro-defined, semantics opaque (R4)
FEATURE [Sketcher::SketchObject] Sketch016
  ExternalGeometry = -> [Box]
  FullyConstrained = true
  MapMode = 5
  Placement = pos=(-157,216,354) rot=(0,0,1;0rad)
  Support = -> [Box]
  sketch-geometry (3):
    g0: LineSegment StartX=115 StartY=19 StartZ=0 EndX=115 EndY=0 EndZ=0
    g1: LineSegment StartX=115 StartY=19 StartZ=0 EndX=230 EndY=19 EndZ=0
    g2: LineSegment StartX=115 StartY=19 StartZ=0 EndX=0 EndY=19 EndZ=0
  constraints (8):
    c: PointOnObject(g0,g-5)
    c: PointOnObject(g0,g-6)
    c: Vertical(g0)
    c: Coincident(g1,g0)
    c: Coincident(g1,g-5)
    c: Coincident(g2,g0)
    c: Coincident(g2,g-5)
    c: Equal(g1,g2)
FEATURE [Part::Feature] Box_cs
  shape: bbox 3e-07 x 19 x 360 mm, 0 faces, 0 solids (baked)
FEATURE [Part::Feature] Box_cs001
  shape: bbox 3e-07 x 19 x 360 mm, 0 faces, 0 solids (baked)
FEATURE [Surface::Filling] Surface006
  Anisotropy = false
  Degree = 3
  Iterations = 2
  MaximumDegree = 8
  MaximumSegments = 9
  PointsOnCurve = 15
  TolAngular = 0.01
  TolCurvature = 0.1
  Tolerance2d = 1e-05
  Tolerance3d = 0.0001
FEATURE [Surface::Filling] Surface005
  Anisotropy = false
  BoundaryEdges = -> [Sketch006]
  BoundaryOrder = [0]
  Degree = 3
  Iterations = 2
  MaximumDegree = 8
  MaximumSegments = 9
  PointsOnCurve = 15
  TolAngular = 0.01
  TolCurvature = 0.1
  Tolerance2d = 1e-05
  Tolerance3d = 0.0001
FEATURE [Surface::Filling] Surface004
  Anisotropy = false
  BoundaryEdges = -> [Sketch010]
  Degree = 3
  Iterations = 2
  MaximumDegree = 8
  MaximumSegments = 9
  PointsOnCurve = 15
  TolAngular = 0.01
  TolCurvature = 0.1
  Tolerance2d = 1e-05
  Tolerance3d = 0.0001
FEATURE [Part::Part2DObjectPython] Line  label="Line_Master_Line"  # Draft 2D object (typed FeaturePython)
  Area = 0
  ChamferSize = 0
  Closed = false
  End = (-42,225.5,174)
  FilletRadius = 0
  Length = 0
  MakeFace = false
  Points = (2) [(-42,225.5,174),(-42,225.5,174)]
  Start = (-42,225.5,174)
  Subdivisions = 0
FEATURE [Part::Part2DObjectPython] Polygon  label="Forme_Polygon"  # Draft 2D object (typed FeaturePython)
  Area = 0
  ChamferSize = 0
  DrawMode = 1
  FacesNumber = 3
  FilletRadius = 0
  MakeFace = false
  Placement = pos=(-42,225.5,174) rot=(0,1,0;2.67794rad)
  Radius = 5
FEATURE [Part::Sweep] Sweep_Externe_
  Frenet = true
  Sections = -> [Polygon]
  Solid = true
  Spine = -> Line
  Transition = 1
FEATURE [App::Part] Part010  label="top"
  Group = -> [Box_cs,Polygon,Sweep_Externe_,Line]
  Origin = -> Origin012
FEATURE [App::Part] Part012  label="top001"
  Group = -> [Part010,Box,Sketch016,Box_cs001,Part,Sketch011]
  Origin = -> Origin014
FEATURE [Sketcher::SketchObject] Sketch017
  FullyConstrained = false
  MapMode = 5
  Placement = pos=(0,0,0) rot=(1,0,0;1.5708rad)
  Support = -> [XZ_Plane016]
  sketch-geometry (4):
    g0: LineSegment StartX=-103.59 StartY=11.0494 StartZ=0 EndX=36.7099 EndY=11.0494 EndZ=0
    g1: LineSegment StartX=36.7099 StartY=11.0494 StartZ=0 EndX=36.7099 EndY=-8.00061 EndZ=0
    g2: LineSegment StartX=36.7099 StartY=-8.00061 StartZ=0 EndX=-103.59 EndY=-8.00061 EndZ=0
    g3: LineSegment StartX=-103.59 StartY=-8.00061 StartZ=0 EndX=-103.59 EndY=11.0494 EndZ=0
  constraints (10):
    c: Coincident(g0,g1)
    c: Coincident(g1,g2)
    c: Coincident(g2,g3)
    c: Coincident(g3,g0)
    c: Horizontal(g0)
    c: Horizontal(g2)
    c: Vertical(g1)
    c: Vertical(g3)
    c: Distance(g3) = 19.05
    c: Distance(g0) = 140.3
FEATURE [Sketcher::SketchObject] Sketch018
  ExternalGeometry = -> [Sketch017]
  FullyConstrained = true
  MapMode = 5
  Placement = pos=(0,0,0) rot=(1,0,0;1.5708rad)
  Support = -> [XZ_Plane016]
  sketch-geometry (4):
    g0: LineSegment StartX=151.01 StartY=11.0494 StartZ=0 EndX=10.7099 EndY=11.0494 EndZ=0
    g1: LineSegment StartX=10.7099 StartY=11.0494 StartZ=0 EndX=10.7099 EndY=-8.00061 EndZ=0
    g2: LineSegment StartX=10.7099 StartY=-8.00061 StartZ=0 EndX=151.01 EndY=-8.00061 EndZ=0
    g3: LineSegment StartX=151.01 StartY=-8.00061 StartZ=0 EndX=151.01 EndY=11.0494 EndZ=0
  constraints (11):
    c: Coincident(g0,g1)
    c: Coincident(g1,g2)
    c: Coincident(g2,g3)
    c: Coincident(g3,g0)
    c: Horizontal(g2)
    c: Vertical(g1)
    c: Vertical(g3)
    c: Equal(g-5,g1)
    c: Equal(g0,g-3)
    c: Tangent(g0,g-3)
    c: Distance(g-5,g0) = 26
FEATURE [Surface::GeomFillSurface] Surface012
  BoundaryList = -> [Sketch017]
  FillType = 0
FEATURE [Surface::GeomFillSurface] Surface013
  BoundaryList = -> [Sketch018]
  FillType = 0
FEATURE [Part::Extrusion] Extrude012
  Base = -> Surface012
  Dir = (0,1,0)
  DirMode = 0
  FaceMakerClass = Part::FaceMakerBullseye
  LengthFwd = 304.8
  LengthRev = 0
  Solid = true
  Symmetric = false
FEATURE [Part::Extrusion] Extrude013
  Base = -> Surface013
  Dir = (0,1,0)
  DirMode = 0
  FaceMakerClass = Part::FaceMakerBullseye
  LengthFwd = 304.8
  LengthRev = 0
  Solid = false
  Symmetric = false
FEATURE [App::Part] Part013
  Group = -> [Sketch017,Sketch018,Surface012,Surface013,Extrude012,Extrude013]
  Origin = -> Origin015
FEATURE [Part::Box] Box001
  AttacherType = Attacher::AttachEngine3D
  Height = 19.05
  Length = 355.6
  Width = 228.6
FEATURE [Sketcher::SketchObject] Sketch019
  FullyConstrained = false
  MapMode = 4
  Placement = pos=(0,0,0) rot=(0.57735,0.57735,0.57735;2.0944rad)
  Support = -> [Box001]
  sketch-geometry (9):
    g0: LineSegment StartX=94.1694 StartY=63.8544 StartZ=0 EndX=94.1694 EndY=47.0374 EndZ=0
    g1: LineSegment StartX=94.1694 StartY=47.0374 StartZ=0 EndX=110.986 EndY=49.1934 EndZ=0
    g2: LineSegment StartX=110.986 StartY=49.1934 StartZ=0 EndX=110.986 EndY=39.4913 EndZ=0
    g3: LineSegment StartX=110.986 StartY=39.4913 StartZ=0 EndX=94.1694 EndY=40.5691 EndZ=0
    g4: LineSegment StartX=94.1694 StartY=40.5691 StartZ=0 EndX=94.1694 EndY=27.6332 EndZ=0
    g5: LineSegment StartX=94.1694 StartY=53.8237 StartZ=0 EndX=120.169 EndY=53.8237 EndZ=0
    g6: LineSegment StartX=120.169 StartY=53.8237 StartZ=0 EndX=120.169 EndY=34.7737 EndZ=0
    g7: LineSegment StartX=120.169 StartY=34.7737 StartZ=0 EndX=94.1694 EndY=34.7737 EndZ=0
    g8: LineSegment StartX=94.1694 StartY=34.7737 StartZ=0 EndX=94.1694 EndY=53.8237 EndZ=0
  constraints (17):
    c: Vertical(g0)
    c: Coincident(g1,g0)
    c: Coincident(g2,g1)
    c: Vertical(g2)
    c: Coincident(g3,g2)
    c: Coincident(g4,g3)
    c: Coincident(g5,g6)
    c: Coincident(g6,g7)
    c: Coincident(g7,g8)
    c: Coincident(g8,g5)
    c: Horizontal(g5)
    c: Horizontal(g7)
    c: Vertical(g6)
    c: DistanceX(g5,g5) = 26
    c: DistanceY(g8,g8) = 19.05
    c: Tangent(g4,g8)
    c: Tangent(g0,g8)
FEATURE [App::Part] Part014  label="good"
  Group = -> [Box001,Sketch019]
  Origin = -> Origin016
FEATURE [Part::Box] Box002
  AttacherType = Attacher::AttachEngine3D
  Height = 19.05
  Length = 355.6
  Width = 228.6
FEATURE [Sketcher::SketchObject] Sketch020
  ExternalGeometry = -> [Box002]
  FullyConstrained = false
  MapMode = 4
  Placement = pos=(0,0,0) rot=(0.57735,0.57735,0.57735;2.0944rad)
  Support = -> [Box002]
  sketch-geometry (1):
    g0: LineSegment StartX=114.3 StartY=19.05 StartZ=0 EndX=114.3 EndY=0.241736 EndZ=0
  constraints (3):
    c: PointOnObject(g0,g-3)
    c: Perpendicular(g-3,g0)
    c: Distance(g0,g-3) = 114.3
FEATURE [App::Part] Part015  label="good001"
  Group = -> [Box002,Sketch020]
  Origin = -> Origin017
FEATURE [App::DocumentObjectGroup] Group  label="top work"
  Group = -> [Part012,Part013,Part014,Part015]
FEATURE [Part::Feature] Face002 .. Face005  x4 (patterned run collapsed; names and placements below)
  shape: bbox 115 x 19 x 3e-07 mm, 1 faces, 0 solids (baked)
FEATURE [Part::Feature] Face006
  Placement = pos=(-157,216,-6) rot=(0.57735,0.57735,0.57735;4.18879rad)
  shape: bbox 2e-07 x 19 x 360 mm, 1 faces, 0 solids (baked)
FEATURE [Part::Feature] Face007
  Placement = pos=(-157,216,-6) rot=(0.57735,0.57735,0.57735;4.18879rad)
  shape: bbox 2e-07 x 19 x 360 mm, 1 faces, 0 solids (baked)
FEATURE [Part::Feature] Face008 .. Face011  x4 (patterned run collapsed; names and placements below)
  shape: bbox 115 x 3e-07 x 360 mm, 1 faces, 0 solids (baked)
FEATURE [Part::Feature] Box_cs002
  shape: bbox 3e-07 x 19 x 360 mm, 0 faces, 0 solids (baked)
FEATURE [Part::Feature] Box_cs003
  shape: bbox 3e-07 x 19 x 360 mm, 0 faces, 0 solids (baked)
FEATURE [Part::Compound] Compound
  Links = -> [Face003,Face005,Face009,Face007,Face011,Box_cs002]
FEATURE [Part::Feature] Compound_solid  label="Compound (Solid)"
  Placement = pos=(0,-161,0) rot=(0,0,1;0rad)
  shape: bbox 115 x 19 x 360 mm, 5 faces (baked)
FEATURE [Part::Compound] Compound001
  Links = -> [Face002,Face004,Face006,Face008,Face010,Box_cs003]
FEATURE [Part::Feature] Compound001_solid  label="Compound001 (Solid)"
  Placement = pos=(0,-308,0) rot=(0,0,1;0rad)
  shape: bbox 115 x 19 x 360 mm, 5 faces (baked)
FEATURE [Part::Compound] Compound002
  Links = -> [Extrude010_solid]
FEATURE [Surface::GeomFillSurface] Surface014
  BoundaryList = -> [Compound001_solid]
  FillType = 0
FEATURE [Surface::GeomFillSurface] Surface015
  BoundaryList = -> [Compound_solid]
  FillType = 0
FEATURE [Part::Compound] Compound003
  Links = -> [Compound_solid,Surface015]
FEATURE [App::Part] Part017
  Group = -> [Face003,Face005,Face007,Face009,Face011,Box_cs002,Compound,Compound_solid,Surface015,Compound003]
  Origin = -> Origin019
  Placement = pos=(0,-147,0) rot=(0,0,1;0rad)
FEATURE [Part::Compound] Compound004
  Links = -> [Surface014,Compound001_solid]
FEATURE [Part::Feature] Compound004_solid  label="Compound004 (Solid)"
  shape: bbox 115 x 19 x 360 mm, 6 faces (baked)
FEATURE [App::Part] Part016  label="piece1"
  Group = -> [Face002,Face004,Face006,Face008,Face010,Box_cs003,Compound001,Compound001_solid,Surface014,Compound004,Compound004_solid]
  Origin = -> Origin018
FEATURE [Part::Box] Box003
  AttacherType = Attacher::AttachEngine3D
  Height = 19
  Length = 360
  Placement = pos=(-157,216,-6) rot=(0.57735,0.57735,0.57735;4.18879rad)
  Width = 230
FEATURE [PartDesign::ShapeBinder] ShapeBinder004
  TraceSupport = false
FEATURE [PartDesign::Body] Body
  Origin = -> Origin
FEATURE [Part::Feature] Wire
  shape: bbox 19.05 x 19.05 x 2e-07 mm, 0 faces, 0 solids (baked)
FEATURE [Part::Feature] Wire001
  Placement = pos=(-244,89,-184) rot=(0,0,-1;1.5708rad)
  shape: bbox 19.69 x 59.95 x 2e-07 mm, 0 faces, 0 solids (baked)
FEATURE [Part::Extrusion] Extrude014
  Base = -> Wire001
  Dir = (0,0,1)
  DirMode = 2
  FaceMakerClass = Part::FaceMakerBullseye
  LengthFwd = 500
  LengthRev = 0
  Placement = pos=(0,77,56) rot=(0,0,1;0rad)
  Solid = false
  Symmetric = false
FEATURE [Part::Feature] Solid  label="penis"
  shape: bbox 115.3 x 19 x 360 mm, 11 faces (baked)
FEATURE [Part::Feature] Solid001  label="vagina"
  shape: bbox 134.4 x 19 x 360 mm, 11 faces (baked)
FEATURE [App::Part] Part018  label="final top"
  Group = -> [Box003,Wire,Wire001,Extrude014,ShapeBinder004,Solid001,Solid]
  Origin = -> Origin020
FEATURE [Part::Feature] Wire002
  Placement = pos=(-244,89,-184) rot=(0,0,-1;1.5708rad)
  shape: bbox 19.69 x 59.95 x 2e-07 mm, 0 faces, 0 solids (baked)
FEATURE [Part::Extrusion] Extrude015
  Base = -> Wire002
  Dir = (0,0,1)
  DirMode = 2
  FaceMakerClass = Part::FaceMakerBullseye
  LengthFwd = 500
  LengthRev = 0
  Placement = pos=(10,-85,157) rot=(-1,0,0;1.5708rad)
  Solid = false
  Symmetric = false
FEATURE [Part::Feature] Wire003
  Placement = pos=(-244,89,-184) rot=(0,0,-1;1.5708rad)
  shape: bbox 19.69 x 59.95 x 2e-07 mm, 0 faces, 0 solids (baked)
FEATURE [Part::Extrusion] Extrude016
  Base = -> Wire003
  Dir = (0,0,1)
  DirMode = 2
  FaceMakerClass = Part::FaceMakerBullseye
  LengthFwd = 500
  LengthRev = 0
  Placement = pos=(10,46.9287,-138.48) rot=(1,0,0;1.5708rad)
  Solid = false
  Symmetric = false
FEATURE [Part::Feature] Solid002  label="penis001"
  shape: bbox 121.4 x 450.9 x 19.05 mm, 29 faces (baked)
FEATURE [Part::Feature] Solid003  label="vagina001"
  shape: bbox 126.8 x 450.8 x 19.05 mm, 34 faces (baked)
FEATURE [App::Part] Part004  label="Left Leg"
  Group = -> [Sketch001,Connect,Extrude001,Sketch002,Face,Extrude002,Extrude,ShapeBinder,ShapeBinder001,Cut,Surface004,Surface005,Surface006,Wire002,Extrude015,Solid003,Solid002]
  Origin = -> Origin005
FEATURE [Part::Feature] Solid004  label="penis002"
  shape: bbox 121.4 x 450.9 x 19.05 mm, 29 faces (baked)
FEATURE [Part::Feature] Solid005  label="vagina002"
  shape: bbox 126.8 x 450.8 x 19.05 mm, 34 faces (baked)
FEATURE [App::Part] Part005  label="Right Leg"
  Group = -> [Sketch004,Connect001,Extrude004,Sketch005,Face001,Extrude005,Extrude003,ShapeBinder002,ShapeBinder003,Cut001,Wire003,Extrude016,Solid004,Solid005]
  Origin = -> Origin006
  Placement = pos=(0,0,303) rot=(0,0,1;0rad)
FEATURE [Sketcher::SketchObject] Sketch
  FullyConstrained = true
  Placement = pos=(0,0,0) rot=(0.57735,0.57735,0.57735;2.0944rad)
FEATURE [App::Part] Part006  label="shelf002"
  Group = -> [Sketch006,Surface,Extrude006,Sketch003,Sketch008,Sketch009,Sketch010,Surface007,Surface008,Extrude007,Extrude008,Cut002,Extrude009,Cut003,Sketch]
  Origin = -> Origin007
  Placement = pos=(380,-184,265) rot=(0,1,0;4.71239rad)
FEATURE [Sketcher::SketchObject] Sketch022  label="holes"
  FullyConstrained = false
  Placement = pos=(0,0,0) rot=(0.57735,0.57735,0.57735;2.0944rad)
  sketch-geometry (8):
    g0: LineSegment StartX=55.7858 StartY=297.719 StartZ=0 EndX=74.8358 EndY=297.719 EndZ=0
    g1: LineSegment StartX=74.8358 StartY=297.719 StartZ=0 EndX=74.8358 EndY=285.019 EndZ=0
    g2: LineSegment StartX=74.8358 StartY=285.019 StartZ=0 EndX=55.7858 EndY=285.019 EndZ=0
    g3: LineSegment StartX=55.7858 StartY=285.019 StartZ=0 EndX=55.7858 EndY=297.719 EndZ=0
    g4: LineSegment StartX=55.7858 StartY=43.7189 StartZ=0 EndX=74.8358 EndY=43.7189 EndZ=0
    g5: LineSegment StartX=74.8358 StartY=43.7189 StartZ=0 EndX=74.8358 EndY=31.0189 EndZ=0
    g6: LineSegment StartX=74.8358 StartY=31.0189 StartZ=0 EndX=55.7858 EndY=31.0189 EndZ=0
    g7: LineSegment StartX=55.7858 StartY=31.0189 StartZ=0 EndX=55.7858 EndY=43.7189 EndZ=0
  constraints (18):
    c: Coincident(g0,g1)
    c: Coincident(g1,g2)
    c: Coincident(g2,g3)
    c: Coincident(g3,g0)
    c: Horizontal(g0)
    c: Horizontal(g2)
    c: Vertical(g1)
    c: Coincident(g4,g5)
    c: Coincident(g5,g6)
    c: Coincident(g6,g7)
    c: Coincident(g7,g4)
    c: Horizontal(g4)
    c: Horizontal(g6)
    c: Vertical(g5)
    c: Equal(g0,g4)
    c: Equal(g3,g7)
    c: Distance(g0) = 19.05
    c: Distance(g3) = 12.7
FEATURE [Part::Feature] Face012
  shape: bbox 2e-07 x 19.05 x 266.7 mm, 2 faces, 0 solids (baked)
FEATURE [Part::Extrusion] Extrude017
  Base = -> Face012
  Dir = (1,0,0)
  DirMode = 2
  FaceMakerClass = Part::FaceMakerBullseye
  LengthFwd = 100
  LengthRev = -2
  Placement = pos=(-425,0,0) rot=(0,0,1;0rad)
  Solid = true
  Symmetric = false
FEATURE [Part::Feature] Face013
  Placement = pos=(-368,0,221) rot=(0,-1,0;1.5708rad)
  shape: bbox 19.05 x 25.4 x 2e-07 mm, 1 faces, 0 solids (baked)
FEATURE [Part::Feature] Face015
  Placement = pos=(-368,0,221) rot=(0,-1,0;1.5708rad)
  shape: bbox 19.05 x 25.4 x 2e-07 mm, 1 faces, 0 solids (baked)
FEATURE [Part::Feature] Face016
  Placement = pos=(-368,0,221) rot=(0,-1,0;1.5708rad)
  shape: bbox 19.05 x 2e-07 x 38.1 mm, 1 faces, 0 solids (baked)
FEATURE [Part::Feature] Face017
  Placement = pos=(-368,0,221) rot=(0,-1,0;1.5708rad)
  shape: bbox 19.05 x 12.7 x 2e-07 mm, 1 faces, 0 solids (baked)
FEATURE [Part::Feature] Face018
  Placement = pos=(-368,0,221) rot=(0,-1,0;1.5708rad)
  shape: bbox 19.05 x 2e-07 x 203.2 mm, 1 faces, 0 solids (baked)
FEATURE [Part::Feature] Face019
  Placement = pos=(-368,0,221) rot=(0,-1,0;1.5708rad)
  shape: bbox 19.05 x 12.7 x 2e-07 mm, 1 faces, 0 solids (baked)
FEATURE [Part::Feature] Face020
  Placement = pos=(-368,0,221) rot=(0,-1,0;1.5708rad)
  shape: bbox 19.05 x 2e-07 x 38.1 mm, 1 faces, 0 solids (baked)
FEATURE [Part::Feature] Face021
  Placement = pos=(-368,0,221) rot=(0,-1,0;1.5708rad)
  shape: bbox 2e-07 x 41.91 x 307.3 mm, 1 faces, 0 solids (baked)
FEATURE [Part::Feature] Face022
  Placement = pos=(-387.05,0,221) rot=(0,-1,0;1.5708rad)
  shape: bbox 2e-07 x 41.91 x 307.3 mm, 1 faces, 0 solids (baked)
FEATURE [Part::Feature] Face023
  Placement = pos=(-368,0,221) rot=(0,-1,0;1.5708rad)
  shape: bbox 19.05 x 2e-07 x 304.8 mm, 1 faces, 0 solids (baked)
FEATURE [Part::Feature] Face024
  Placement = pos=(-368,0,221) rot=(0,-1,0;1.5708rad)
  shape: bbox 19.05 x 38.1 x 2e-07 mm, 1 faces, 0 solids (baked)
FEATURE [Part::Feature] Face025
  Placement = pos=(-368,0,221) rot=(0,-1,0;1.5708rad)
  shape: bbox 19.05 x 2e-07 x 12.7 mm, 1 faces, 0 solids (baked)
FEATURE [Part::Feature] Face026
  Placement = pos=(-368,0,221) rot=(0,-1,0;1.5708rad)
  shape: bbox 19.05 x 2e-07 x 12.7 mm, 1 faces, 0 solids (baked)
FEATURE [Part::Feature] Face027
  Placement = pos=(-368,0,221) rot=(0,-1,0;1.5708rad)
  shape: bbox 19.05 x 38.1 x 2e-07 mm, 1 faces, 0 solids (baked)
FEATURE [Part::Feature] Face028
  Placement = pos=(-368,0,221) rot=(0,-1,0;1.5708rad)
  shape: bbox 2e-07 x 41.91 x 335.3 mm, 1 faces, 0 solids (baked)
FEATURE [Part::Feature] Face029
  Placement = pos=(-387.05,0,221) rot=(0,-1,0;1.5708rad)
  shape: bbox 2e-07 x 41.91 x 335.3 mm, 1 faces, 0 solids (baked)
FEATURE [Part::Feature] Subtraction
  shape: bbox 19.05 x 25.4 x 2e-07 mm, 1 faces, 0 solids (baked)
FEATURE [Part::Feature] Face014
  Placement = pos=(-368,0,221) rot=(0,-1,0;1.5708rad)
  shape: bbox 19.05 x 2e-07 x 279.4 mm, 1 faces, 0 solids (baked)
FEATURE [Part::Part2DObjectPython] Wire004  # Draft 2D object (typed FeaturePython)
  Area = 21290.3
  ChamferSize = 0
  Closed = true
  End = (-368,93.8858,316.769)
  FilletRadius = 0
  Length = 762
  MakeFace = true
  Points = (12) [(-368,55.7858,316.769),(-368,55.7858,304.069),(-368,30.3858,304.069),(-368,30.3858,265.969),(-368,17.6858,265.969),(-368,17.6858,62.7689),+6 more]
  Start = (-368,55.7858,316.769)
  Subdivisions = 0
FEATURE [Part::Extrusion] Extrude018
  Base = -> Wire004
  Dir = (1,0,0)
  DirMode = 0
  FaceMakerClass = Part::FaceMakerBullseye
  LengthFwd = 19.05
  LengthRev = 0
  Solid = true
  Symmetric = false
FEATURE [Part::Extrusion] Extrude019
  Base = -> Wire004
  Dir = (1,0,0)
  DirMode = 0
  FaceMakerClass = Part::FaceMakerBullseye
  LengthFwd = 19.05
  LengthRev = 0
  Solid = true
  Symmetric = false
FEATURE [Part::Cut] Cut004
  Base = -> Extrude019
  Tool = -> Extrude017
FEATURE [Part::Compound] Compound005  label="rail with holes"
  Links = -> [Cut004]
FEATURE [Sketcher::SketchObject] Sketch023
  FullyConstrained = true
  Placement = pos=(0,0,0) rot=(0.57735,0.57735,0.57735;2.0944rad)
FEATURE [App::Part] Part019
  Group = -> [Face013,Face014,Face015,Face016,Face017,Face018,Face019,Face020,Face021,Face023,Face022,Face024,Face025,Face026,Face027,Face028,Face029,Subtraction,Sketch023]
  Origin = -> Origin021
FEATURE [App::Part] Part011  label="Rail Sketch"
  Group = -> [Extrude010_solid,Compound002,Sketch022,Face012,Extrude017,Part019,Wire004,Extrude018,Extrude019,Cut004,Compound005]
  Origin = -> Origin013
FEATURE [Sketcher::SketchObject] Sketch014
  FullyConstrained = false
  MapMode = 2
  Support = -> [Part011]
  sketch-geometry (15):
    g0: LineSegment StartX=95.7689 StartY=93.8858 StartZ=0 EndX=95.7689 EndY=55.7858 EndZ=0
    g1: LineSegment StartX=95.7689 StartY=55.7858 StartZ=0 EndX=83.0689 EndY=55.7858 EndZ=0
    g2: LineSegment StartX=83.0689 StartY=55.7858 StartZ=0 EndX=83.0689 EndY=30.3858 EndZ=0
    g3: LineSegment StartX=83.0689 StartY=30.3858 StartZ=0 EndX=44.9689 EndY=30.3858 EndZ=0
    g4: LineSegment StartX=44.9689 StartY=30.3858 StartZ=0 EndX=44.9689 EndY=17.6858 EndZ=0
    g5: LineSegment StartX=-158.231 StartY=17.6858 StartZ=0 EndX=-158.231 EndY=30.3858 EndZ=0
    g6: LineSegment StartX=-158.231 StartY=30.3858 StartZ=0 EndX=-196.331 EndY=30.3858 EndZ=0
    g7: LineSegment StartX=-196.331 StartY=30.3858 StartZ=0 EndX=-196.331 EndY=55.7858 EndZ=0
    g8: LineSegment StartX=-196.331 StartY=55.7858 StartZ=0 EndX=-209.031 EndY=55.7858 EndZ=0
    g9: LineSegment StartX=-209.031 StartY=55.7858 StartZ=0 EndX=-209.031 EndY=93.8858 EndZ=0
    g10: LineSegment StartX=-209.031 StartY=93.8858 StartZ=0 EndX=95.7689 EndY=93.8858 EndZ=0
    g11: LineSegment StartX=-196.331 StartY=55.7858 StartZ=0 EndX=83.0689 EndY=55.7858 EndZ=0
    g12: LineSegment StartX=-177.281 StartY=93.8858 StartZ=0 EndX=-177.281 EndY=30.3858 EndZ=0
    g13: LineSegment StartX=64.0189 StartY=93.8858 StartZ=0 EndX=64.0189 EndY=30.3858 EndZ=0
    g14: LineSegment StartX=-158.231 StartY=17.6858 StartZ=0 EndX=44.9689 EndY=17.6858 EndZ=0
  constraints (43):
    c: Vertical(g0)
    c: Coincident(g0,g1)
    c: Coincident(g1,g2)
    c: Vertical(g2)
    c: Coincident(g2,g3)
    c: Horizontal(g3)
    c: Coincident(g3,g4)
    c: Vertical(g4)
    c: Coincident(g5,g6)
    c: Horizontal(g6)
    c: Coincident(g6,g7)
    c: Vertical(g7)
    c: Coincident(g7,g8)
    c: Coincident(g8,g9)
    c: Coincident(g9,g10)
    c: Horizontal(g10)
    c: Distance(g9,g0) = 304.8
    c: Perpendicular(g10,g9)
    c: Distance(g9) = 38.1
    c: Equal(g9,g0)
    c: Perpendicular(g9,g8)
    c: Perpendicular(g0,g1)
    c: Equal(g8,g1)
    c: Distance(g8) = 12.7
    c: Equal(g7,g2)
    c: Distance(g5,g10) = 76.2
    c: Distance(g5) = 12.7
    c: Equal(g3,g6)
    c: DistanceX(g8,g5) = 50.8
    c: Coincident(g11,g7)
    c: Coincident(g11,g1)
    c: PointOnObject(g12,g10)
    c: PointOnObject(g12,g6)
    c: Vertical(g12)
    c: PointOnObject(g13,g3)
    c: Distance(g12,g5) = 19.05
    c: Distance(g13,g3) = 19.05
    c: Coincident(g0,g10)
    c: PointOnObject(g13,g10)
    c: Perpendicular(g10,g13)
    c: Coincident(g14,g5)
    c: Coincident(g14,g4)
    c: Horizontal(g14)
FEATURE [Surface::Filling] Surface009
  Anisotropy = false
  BoundaryEdges = -> [Sketch014]
  BoundaryOrder = [0,0,0,0,0,0]
  Degree = 3
  Iterations = 2
  MaximumDegree = 8
  MaximumSegments = 9
  PointsOnCurve = 15
  TolAngular = 0.01
  TolCurvature = 0.1
  Tolerance2d = 1e-05
  Tolerance3d = 0.0001
FEATURE [Surface::Filling] Surface010  label="Surface0109"
  Anisotropy = false
  BoundaryEdges = -> [Sketch014]
  BoundaryOrder = [0,0,0,0,0,0,0,0]
  Degree = 3
  Iterations = 2
  MaximumDegree = 8
  MaximumSegments = 9
  PointsOnCurve = 15
  TolAngular = 0.01
  TolCurvature = 0.1
  Tolerance2d = 1e-05
  Tolerance3d = 0.0001
FEATURE [Part::MultiFuse] Fusion
  Shapes = -> [Surface010,Surface009]
FEATURE [Part::Extrusion] Extrude010
  Base = -> Fusion
  Dir = (0,0,1)
  DirMode = 0
  FaceMakerClass = Part::FaceMakerBullseye
  LengthFwd = 19.05
  LengthRev = 0
  Placement = pos=(-368,0,102) rot=(0,-1,0;1.5708rad)
  Solid = false
  Symmetric = false
FEATURE [Part::Extrusion] Extrude011
  Base = -> Fusion
  Dir = (0,0,1)
  DirMode = 0
  FaceMakerClass = Part::FaceMakerBullseye
  LengthFwd = 19.05
  LengthRev = 0
  Solid = true
  Symmetric = false
FEATURE [Sketcher::SketchObject] Sketch015
  FullyConstrained = true
  MapMode = 4
  Placement = pos=(0,0,0) rot=(0.57735,0.57735,0.57735;2.0944rad)
  Support = -> [Part011]
FEATURE [Part::Feature] Extrude015_solid  label="Extrude015 (Solid)"
  shape: bbox 19.69 x 500 x 59.95 mm, 6 faces (baked)
FEATURE [Part::Feature] Wire006  label=".91mm"
  shape: bbox 34.82 x 19.05 x 2e-07 mm, 0 faces, 0 solids (baked)
FEATURE [Part::Feature] Wire005  label="1.04mm"
  shape: bbox 34.82 x 19.05 x 2e-07 mm, 0 faces, 0 solids (baked)
FEATURE [Part::Feature] Wire007  label=".78mm"
  shape: bbox 34.82 x 19.05 x 2e-07 mm, 0 faces, 0 solids (baked)
FEATURE [Part::Feature] Wire008  label=".52mm"
  shape: bbox 34.82 x 19.05 x 2e-07 mm, 0 faces, 0 solids (baked)
FEATURE [Part::Feature] Wire009  label=".39mm"
  shape: bbox 34.82 x 19.05 x 2e-07 mm, 0 faces, 0 solids (baked)
FEATURE [Part::Feature] Wire011  label=".13mm"
  shape: bbox 34.82 x 19.05 x 2e-07 mm, 0 faces, 0 solids (baked)
FEATURE [Part::Feature] Wire010  label=".26mm"
  shape: bbox 34.82 x 19.05 x 2e-07 mm, 0 faces, 0 solids (baked)
FEATURE [Part::Feature] Wire012  label=".65mm"
  shape: bbox 34.82 x 19.05 x 2e-07 mm, 0 faces, 0 solids (baked)
FEATURE [App::Part] Part020  label="dovetail"
  Group = -> [Wire005,Wire006,Wire007,Wire008,Wire009,Wire010,Wire011,Wire012]
  Origin = -> Origin022
FEATURE [Part::Feature] Shape  label="Solid"
  Placement = pos=(10,46.9287,-138.48) rot=(1,0,0;1.5708rad)
  shape: bbox 21.77 x 502.1 x 62.03 mm, 6 faces, 0 solids (baked)
FEATURE [Part::Feature] Shape001  label="Solid001"
  Placement = pos=(10,46.9287,-138.48) rot=(1,0,0;1.5708rad)
  shape: bbox 21.77 x 502.1 x 62.03 mm, 6 faces, 0 solids (baked)
FEATURE [Part::Feature] Shell
  shape: bbox 24.13 x 24.13 x 3 mm, 434 faces (baked)
FEATURE [Mesh::Feature] logo_Result
FEATURE [App::FeaturePython] logo_Mesh  # WARN: FeaturePython — macro-defined, semantics opaque (R4)
  LithophaneImage = -> logo
  Result = -> logo_Result
FEATURE [Sketcher::SketchObject] Sketch024
  FullyConstrained = false
  MapMode = 4
  Placement = pos=(0,0,0) rot=(0.57735,0.57735,0.57735;2.0944rad)
  Support = -> [Shell]
  sketch-geometry (1):
    g0: LineSegment StartX=-1.10621 StartY=1.24668 StartZ=0 EndX=25.9943 EndY=1.24668 EndZ=0
  constraints (1):
    c: Horizontal(g0)
FEATURE [Part::Extrusion] Extrude020
  Base = -> Sketch024
  Dir = (1,0,0)
  DirMode = 2
  FaceMakerClass = Part::FaceMakerBullseye
  LengthFwd = 30
  LengthRev = 0
  Solid = false
  Symmetric = false
FEATURE [Part::Feature] Extrude010_solid001  label="Extrude010 (Solid)001"
  Placement = pos=(0,0,119) rot=(0,0,1;0rad)
  shape: bbox 19.05 x 80.33 x 335.3 mm, 17 faces (baked)
FEATURE [Part::Compound] Compound006
  Links = -> [Extrude010_solid001]
FEATURE [Part::Feature] Face030
  shape: bbox 2e-07 x 19.05 x 266.7 mm, 2 faces, 0 solids (baked)
FEATURE [Part::Extrusion] Extrude022
  Base = -> Face030
  Dir = (1,0,0)
  DirMode = 2
  FaceMakerClass = Part::FaceMakerBullseye
  LengthFwd = 100
  LengthRev = -2
  Placement = pos=(-425,0,0) rot=(0,0,1;0rad)
  Solid = true
  Symmetric = false
FEATURE [Part::Feature] Face031
  Placement = pos=(-368,0,221) rot=(0,-1,0;1.5708rad)
  shape: bbox 19.05 x 25.4 x 2e-07 mm, 1 faces, 0 solids (baked)
FEATURE [Part::Feature] Face032
  Placement = pos=(-368,0,221) rot=(0,-1,0;1.5708rad)
  shape: bbox 19.05 x 2e-07 x 279.4 mm, 1 faces, 0 solids (baked)
FEATURE [Part::Feature] Face033
  Placement = pos=(-368,0,221) rot=(0,-1,0;1.5708rad)
  shape: bbox 19.05 x 25.4 x 2e-07 mm, 1 faces, 0 solids (baked)
FEATURE [Part::Feature] Face034
  Placement = pos=(-368,0,221) rot=(0,-1,0;1.5708rad)
  shape: bbox 19.05 x 2e-07 x 38.1 mm, 1 faces, 0 solids (baked)
FEATURE [Part::Feature] Face035
  Placement = pos=(-368,0,221) rot=(0,-1,0;1.5708rad)
  shape: bbox 19.05 x 12.7 x 2e-07 mm, 1 faces, 0 solids (baked)
FEATURE [Part::Feature] Face036
  Placement = pos=(-368,0,221) rot=(0,-1,0;1.5708rad)
  shape: bbox 19.05 x 2e-07 x 203.2 mm, 1 faces, 0 solids (baked)
FEATURE [Part::Feature] Face037
  Placement = pos=(-368,0,221) rot=(0,-1,0;1.5708rad)
  shape: bbox 19.05 x 12.7 x 2e-07 mm, 1 faces, 0 solids (baked)
FEATURE [Part::Feature] Face038
  Placement = pos=(-368,0,221) rot=(0,-1,0;1.5708rad)
  shape: bbox 19.05 x 2e-07 x 38.1 mm, 1 faces, 0 solids (baked)
FEATURE [Part::Feature] Face039
  Placement = pos=(-368,0,221) rot=(0,-1,0;1.5708rad)
  shape: bbox 2e-07 x 41.91 x 307.3 mm, 1 faces, 0 solids (baked)
FEATURE [Part::Feature] Face040
  Placement = pos=(-387.05,0,221) rot=(0,-1,0;1.5708rad)
  shape: bbox 2e-07 x 41.91 x 307.3 mm, 1 faces, 0 solids (baked)
FEATURE [Part::Feature] Face041
  Placement = pos=(-368,0,221) rot=(0,-1,0;1.5708rad)
  shape: bbox 19.05 x 2e-07 x 304.8 mm, 1 faces, 0 solids (baked)
FEATURE [Part::Feature] Face042
  Placement = pos=(-368,0,221) rot=(0,-1,0;1.5708rad)
  shape: bbox 19.05 x 38.1 x 2e-07 mm, 1 faces, 0 solids (baked)
FEATURE [Part::Feature] Face043
  Placement = pos=(-368,0,221) rot=(0,-1,0;1.5708rad)
  shape: bbox 19.05 x 2e-07 x 12.7 mm, 1 faces, 0 solids (baked)
FEATURE [Part::Feature] Face044
  Placement = pos=(-368,0,221) rot=(0,-1,0;1.5708rad)
  shape: bbox 19.05 x 2e-07 x 12.7 mm, 1 faces, 0 solids (baked)
FEATURE [Part::Feature] Face045
  Placement = pos=(-368,0,221) rot=(0,-1,0;1.5708rad)
  shape: bbox 19.05 x 38.1 x 2e-07 mm, 1 faces, 0 solids (baked)
FEATURE [Part::Feature] Face046
  Placement = pos=(-368,0,221) rot=(0,-1,0;1.5708rad)
  shape: bbox 2e-07 x 41.91 x 335.3 mm, 1 faces, 0 solids (baked)
FEATURE [Part::Feature] Face047
  Placement = pos=(-387.05,0,221) rot=(0,-1,0;1.5708rad)
  shape: bbox 2e-07 x 41.91 x 335.3 mm, 1 faces, 0 solids (baked)
FEATURE [Sketcher::SketchObject] Sketch026  label="holes001"
  FullyConstrained = false
  Placement = pos=(0,0,0) rot=(0.57735,0.57735,0.57735;2.0944rad)
  sketch-geometry (8):
    g0: LineSegment StartX=55.7858 StartY=297.719 StartZ=0 EndX=74.8358 EndY=297.719 EndZ=0
    g1: LineSegment StartX=74.8358 StartY=297.719 StartZ=0 EndX=74.8358 EndY=285.019 EndZ=0
    g2: LineSegment StartX=74.8358 StartY=285.019 StartZ=0 EndX=55.7858 EndY=285.019 EndZ=0
    g3: LineSegment StartX=55.7858 StartY=285.019 StartZ=0 EndX=55.7858 EndY=297.719 EndZ=0
    g4: LineSegment StartX=55.7858 StartY=43.7189 StartZ=0 EndX=74.8358 EndY=43.7189 EndZ=0
    g5: LineSegment StartX=74.8358 StartY=43.7189 StartZ=0 EndX=74.8358 EndY=31.0189 EndZ=0
    g6: LineSegment StartX=74.8358 StartY=31.0189 StartZ=0 EndX=55.7858 EndY=31.0189 EndZ=0
    g7: LineSegment StartX=55.7858 StartY=31.0189 StartZ=0 EndX=55.7858 EndY=43.7189 EndZ=0
  constraints (18):
    c: Coincident(g0,g1)
    c: Coincident(g1,g2)
    c: Coincident(g2,g3)
    c: Coincident(g3,g0)
    c: Horizontal(g0)
    c: Horizontal(g2)
    c: Vertical(g1)
    c: Coincident(g4,g5)
    c: Coincident(g5,g6)
    c: Coincident(g6,g7)
    c: Coincident(g7,g4)
    c: Horizontal(g4)
    c: Horizontal(g6)
    c: Vertical(g5)
    c: Equal(g0,g4)
    c: Equal(g3,g7)
    c: Distance(g0) = 19.05
    c: Distance(g3) = 12.7
FEATURE [Sketcher::SketchObject] Sketch027
  FullyConstrained = true
  Placement = pos=(0,0,0) rot=(0.57735,0.57735,0.57735;2.0944rad)
FEATURE [Part::Feature] Subtraction001
  shape: bbox 19.05 x 25.4 x 2e-07 mm, 1 faces, 0 solids (baked)
FEATURE [App::Part] Part022
  Group = -> [Face031,Face032,Face033,Face034,Face035,Face036,Face037,Face038,Face039,Face041,Face040,Face042,Face043,Face044,Face045,Face046,Face047,Subtraction001,Sketch027]
  Origin = -> Origin024
FEATURE [Part::Part2DObjectPython] Wire013  # Draft 2D object (typed FeaturePython)
  Area = 21290.3
  ChamferSize = 0
  Closed = true
  End = (-368,93.8858,316.769)
  FilletRadius = 0
  Length = 762
  MakeFace = true
  Points = (12) [(-368,55.7858,316.769),(-368,55.7858,304.069),(-368,30.3858,304.069),(-368,30.3858,265.969),(-368,17.6858,265.969),(-368,17.6858,62.7689),+6 more]
  Start = (-368,55.7858,316.769)
  Subdivisions = 0
FEATURE [Part::Extrusion] Extrude023
  Base = -> Wire013
  Dir = (1,0,0)
  DirMode = 0
  FaceMakerClass = Part::FaceMakerBullseye
  LengthFwd = 19.05
  LengthRev = 0
  Solid = true
  Symmetric = false
FEATURE [Part::Extrusion] Extrude024
  Base = -> Wire013
  Dir = (1,0,0)
  DirMode = 0
  FaceMakerClass = Part::FaceMakerBullseye
  LengthFwd = 19.05
  LengthRev = 0
  Solid = true
  Symmetric = false
FEATURE [Part::Cut] Cut005
  Base = -> Extrude024
  Tool = -> Extrude022
FEATURE [Part::Compound] Compound007  label="rail with holes001"
  Links = -> [Cut005]
FEATURE [App::Part] Part021  label="Rail Sketch001"
  Group = -> [Extrude010_solid001,Compound006,Sketch026,Face030,Extrude022,Part022,Wire013,Extrude023,Extrude024,Cut005,Compound007]
  Origin = -> Origin023
FEATURE [Sketcher::SketchObject] Sketch025
  FullyConstrained = false
  MapMode = 2
  Support = -> [Part021]
  sketch-geometry (15):
    g0: LineSegment StartX=95.7689 StartY=93.8858 StartZ=0 EndX=95.7689 EndY=55.7858 EndZ=0
    g1: LineSegment StartX=95.7689 StartY=55.7858 StartZ=0 EndX=83.0689 EndY=55.7858 EndZ=0
    g2: LineSegment StartX=83.0689 StartY=55.7858 StartZ=0 EndX=83.0689 EndY=30.3858 EndZ=0
    g3: LineSegment StartX=83.0689 StartY=30.3858 StartZ=0 EndX=44.9689 EndY=30.3858 EndZ=0
    g4: LineSegment StartX=44.9689 StartY=30.3858 StartZ=0 EndX=44.9689 EndY=17.6858 EndZ=0
    g5: LineSegment StartX=-158.231 StartY=17.6858 StartZ=0 EndX=-158.231 EndY=30.3858 EndZ=0
    g6: LineSegment StartX=-158.231 StartY=30.3858 StartZ=0 EndX=-196.331 EndY=30.3858 EndZ=0
    g7: LineSegment StartX=-196.331 StartY=30.3858 StartZ=0 EndX=-196.331 EndY=55.7858 EndZ=0
    g8: LineSegment StartX=-196.331 StartY=55.7858 StartZ=0 EndX=-209.031 EndY=55.7858 EndZ=0
    g9: LineSegment StartX=-209.031 StartY=55.7858 StartZ=0 EndX=-209.031 EndY=93.8858 EndZ=0
    g10: LineSegment StartX=-209.031 StartY=93.8858 StartZ=0 EndX=95.7689 EndY=93.8858 EndZ=0
    g11: LineSegment StartX=-196.331 StartY=55.7858 StartZ=0 EndX=83.0689 EndY=55.7858 EndZ=0
    g12: LineSegment StartX=-177.281 StartY=93.8858 StartZ=0 EndX=-177.281 EndY=30.3858 EndZ=0
    g13: LineSegment StartX=64.0189 StartY=93.8858 StartZ=0 EndX=64.0189 EndY=30.3858 EndZ=0
    g14: LineSegment StartX=-158.231 StartY=17.6858 StartZ=0 EndX=44.9689 EndY=17.6858 EndZ=0
  constraints (43):
    c: Vertical(g0)
    c: Coincident(g0,g1)
    c: Coincident(g1,g2)
    c: Vertical(g2)
    c: Coincident(g2,g3)
    c: Horizontal(g3)
    c: Coincident(g3,g4)
    c: Vertical(g4)
    c: Coincident(g5,g6)
    c: Horizontal(g6)
    c: Coincident(g6,g7)
    c: Vertical(g7)
    c: Coincident(g7,g8)
    c: Coincident(g8,g9)
    c: Coincident(g9,g10)
    c: Horizontal(g10)
    c: Distance(g9,g0) = 304.8
    c: Perpendicular(g10,g9)
    c: Distance(g9) = 38.1
    c: Equal(g9,g0)
    c: Perpendicular(g9,g8)
    c: Perpendicular(g0,g1)
    c: Equal(g8,g1)
    c: Distance(g8) = 12.7
    c: Equal(g7,g2)
    c: Distance(g5,g10) = 76.2
    c: Distance(g5) = 12.7
    c: Equal(g3,g6)
    c: DistanceX(g8,g5) = 50.8
    c: Coincident(g11,g7)
    c: Coincident(g11,g1)
    c: PointOnObject(g12,g10)
    c: PointOnObject(g12,g6)
    c: Vertical(g12)
    c: PointOnObject(g13,g3)
    c: Distance(g12,g5) = 19.05
    c: Distance(g13,g3) = 19.05
    c: Coincident(g0,g10)
    c: PointOnObject(g13,g10)
    c: Perpendicular(g10,g13)
    c: Coincident(g14,g5)
    c: Coincident(g14,g4)
    c: Horizontal(g14)
FEATURE [Surface::Filling] Surface016
  Anisotropy = false
  BoundaryEdges = -> [Sketch025]
  BoundaryOrder = [0,0,0,0,0,0]
  Degree = 3
  Iterations = 2
  MaximumDegree = 8
  MaximumSegments = 9
  PointsOnCurve = 15
  TolAngular = 0.01
  TolCurvature = 0.1
  Tolerance2d = 1e-05
  Tolerance3d = 0.0001
FEATURE [Surface::Filling] Surface017
  Anisotropy = false
  BoundaryEdges = -> [Sketch025]
  BoundaryOrder = [0,0,0,0,0,0,0,0]
  Degree = 3
  Iterations = 2
  MaximumDegree = 8
  MaximumSegments = 9
  PointsOnCurve = 15
  TolAngular = 0.01
  TolCurvature = 0.1
  Tolerance2d = 1e-05
  Tolerance3d = 0.0001
FEATURE [Part::MultiFuse] Fusion001
  Shapes = -> [Surface017,Surface016]
FEATURE [Part::Extrusion] Extrude021
  Base = -> Fusion001
  Dir = (0,0,1)
  DirMode = 0
  FaceMakerClass = Part::FaceMakerBullseye
  LengthFwd = 19.05
  LengthRev = 0
  Solid = true
  Symmetric = false
FEATURE [Sketcher::SketchObject] Sketch028  label="shelf003"
  FullyConstrained = false
  MapMode = 5
  Placement = pos=(0,0,0) rot=(1,0,0;1.5708rad)
  Support = -> [XZ_Plane026]
  sketch-geometry (19):
    g0: LineSegment StartX=-202.002 StartY=139.919 StartZ=0 EndX=-202.002 EndY=63.7195 EndZ=0
    g1: LineSegment StartX=-202.002 StartY=63.7195 StartZ=0 EndX=-252.802 EndY=63.7195 EndZ=0
    g2: LineSegment StartX=-252.802 StartY=63.7195 StartZ=0 EndX=-252.802 EndY=139.919 EndZ=0
    g3: LineSegment StartX=-252.802 StartY=139.919 StartZ=0 EndX=-202.002 EndY=139.919 EndZ=0
    g4: LineSegment StartX=-202.002 StartY=139.919 StartZ=0 EndX=-202.002 EndY=171.669 EndZ=0
    g5: LineSegment StartX=-202.002 StartY=63.7195 StartZ=0 EndX=-202.002 EndY=31.9695 EndZ=0
    g6: LineSegment StartX=1.18793 StartY=171.669 StartZ=0 EndX=1.18793 EndY=139.919 EndZ=0
    g7: LineSegment StartX=1.18793 StartY=139.919 StartZ=0 EndX=51.9879 EndY=139.919 EndZ=0
    g8: LineSegment StartX=51.9879 StartY=139.919 StartZ=0 EndX=51.9879 EndY=63.7195 EndZ=0
    g9: LineSegment StartX=51.9879 StartY=63.7195 StartZ=0 EndX=1.18793 EndY=63.7195 EndZ=0
    g10: LineSegment StartX=1.18793 StartY=63.7195 StartZ=0 EndX=1.18793 EndY=31.9695 EndZ=0
    g11: LineSegment StartX=-202.002 StartY=171.669 StartZ=0 EndX=1.18793 EndY=171.669 EndZ=0
    g12: LineSegment StartX=-202.002 StartY=31.9695 StartZ=0 EndX=1.18793 EndY=31.9695 EndZ=0
    g13: LineSegment StartX=1.18793 StartY=139.919 StartZ=0 EndX=1.18793 EndY=63.7195 EndZ=0
    g14: LineSegment StartX=-221.052 StartY=139.919 StartZ=0 EndX=-221.052 EndY=63.7195 EndZ=0
    g15: LineSegment StartX=20.2379 StartY=139.919 StartZ=0 EndX=20.2379 EndY=63.7195 EndZ=0
    g16: LineSegment StartX=20.2379 StartY=63.7195 StartZ=0 EndX=0.408682 EndY=63.7195 EndZ=0
    g17: LineSegment StartX=51.9879 StartY=63.7195 StartZ=0 EndX=20.2379 EndY=63.7195 EndZ=0
    g18: LineSegment StartX=-221.052 StartY=63.7195 StartZ=0 EndX=-252.802 EndY=63.7195 EndZ=0
  constraints (51):
    c: Vertical(g0)
    c: Coincident(g1,g0)
    c: Horizontal(g1)
    c: Coincident(g2,g1)
    c: Vertical(g2)
    c: Coincident(g3,g2)
    c: Coincident(g3,g0)
    c: Horizontal(g3)
    c: Distance(g2) = 76.2
    c: Distance(g3) = 50.8
    c: Perpendicular(g3,g4)
    c: Coincident(g4,g0)
    c: Coincident(g5,g0)
    c: Vertical(g5)
    c: Equal(g5,g4)
    c: Vertical(g6)
    c: Coincident(g7,g6)
    c: Horizontal(g7)
    c: Coincident(g8,g7)
    c: Vertical(g8)
    c: Coincident(g9,g8)
    c: Horizontal(g9)
    c: Coincident(g10,g9)
    c: Vertical(g10)
    c: Distance(g2,g7) = 304.79
    c: Coincident(g11,g4)
    c: Coincident(g11,g6)
    c: Horizontal(g11)
    c: Coincident(g12,g5)
    c: Coincident(g12,g10)
    c: Horizontal(g12)
    c: Equal(g6,g10)
    c: Equal(g10,g5)
    c: Equal(g3,g7)
    c: Equal(g7,g9)
    c: Coincident(g13,g6)
    c: Coincident(g13,g9)
    c: PointOnObject(g14,g3)
    c: PointOnObject(g14,g1)
    c: Vertical(g14)
    c: PointOnObject(g15,g7)
    c: PointOnObject(g15,g9)
    c: Vertical(g15)
    c: Distance(g14,g1) = 31.75
    c: Coincident(g16,g15)
    c: Coincident(g17,g8)
    c: Coincident(g17,g15)
    c: Coincident(g18,g14)
    c: Coincident(g18,g1)
    c: Equal(g17,g18)
    c: Distance(g6,g10) = 139.7
FEATURE [Sketcher::SketchObject] Sketch029  label="shelf004"
  FullyConstrained = false
  MapMode = 5
  Placement = pos=(0,0,0) rot=(1,0,0;1.5708rad)
  Support = -> [XZ_Plane027]
  sketch-geometry (19):
    g0: LineSegment StartX=-202.002 StartY=139.919 StartZ=0 EndX=-202.002 EndY=63.7195 EndZ=0
    g1: LineSegment StartX=-202.002 StartY=63.7195 StartZ=0 EndX=-252.802 EndY=63.7195 EndZ=0
    g2: LineSegment StartX=-252.802 StartY=63.7195 StartZ=0 EndX=-252.802 EndY=139.919 EndZ=0
    g3: LineSegment StartX=-252.802 StartY=139.919 StartZ=0 EndX=-202.002 EndY=139.919 EndZ=0
    g4: LineSegment StartX=-202.002 StartY=139.919 StartZ=0 EndX=-202.002 EndY=171.669 EndZ=0
    g5: LineSegment StartX=-202.002 StartY=63.7195 StartZ=0 EndX=-202.002 EndY=31.9695 EndZ=0
    g6: LineSegment StartX=1.18793 StartY=171.669 StartZ=0 EndX=1.18793 EndY=139.919 EndZ=0
    g7: LineSegment StartX=1.18793 StartY=139.919 StartZ=0 EndX=51.9879 EndY=139.919 EndZ=0
    g8: LineSegment StartX=51.9879 StartY=139.919 StartZ=0 EndX=51.9879 EndY=63.7195 EndZ=0
    g9: LineSegment StartX=51.9879 StartY=63.7195 StartZ=0 EndX=1.18793 EndY=63.7195 EndZ=0
    g10: LineSegment StartX=1.18793 StartY=63.7195 StartZ=0 EndX=1.18793 EndY=31.9695 EndZ=0
    g11: LineSegment StartX=-202.002 StartY=171.669 StartZ=0 EndX=1.18793 EndY=171.669 EndZ=0
    g12: LineSegment StartX=-202.002 StartY=31.9695 StartZ=0 EndX=1.18793 EndY=31.9695 EndZ=0
    g13: LineSegment StartX=1.18793 StartY=139.919 StartZ=0 EndX=1.18793 EndY=63.7195 EndZ=0
    g14: LineSegment StartX=-221.052 StartY=139.919 StartZ=0 EndX=-221.052 EndY=63.7195 EndZ=0
    g15: LineSegment StartX=20.2379 StartY=139.919 StartZ=0 EndX=20.2379 EndY=63.7195 EndZ=0
    g16: LineSegment StartX=20.2379 StartY=63.7195 StartZ=0 EndX=0.408682 EndY=63.7195 EndZ=0
    g17: LineSegment StartX=51.9879 StartY=63.7195 StartZ=0 EndX=20.2379 EndY=63.7195 EndZ=0
    g18: LineSegment StartX=-221.052 StartY=63.7195 StartZ=0 EndX=-252.802 EndY=63.7195 EndZ=0
  constraints (51):
    c: Vertical(g0)
    c: Coincident(g1,g0)
    c: Horizontal(g1)
    c: Coincident(g2,g1)
    c: Vertical(g2)
    c: Coincident(g3,g2)
    c: Coincident(g3,g0)
    c: Horizontal(g3)
    c: Distance(g2) = 76.2
    c: Distance(g3) = 50.8
    c: Perpendicular(g3,g4)
    c: Coincident(g4,g0)
    c: Coincident(g5,g0)
    c: Vertical(g5)
    c: Equal(g5,g4)
    c: Vertical(g6)
    c: Coincident(g7,g6)
    c: Horizontal(g7)
    c: Coincident(g8,g7)
    c: Vertical(g8)
    c: Coincident(g9,g8)
    c: Horizontal(g9)
    c: Coincident(g10,g9)
    c: Vertical(g10)
    c: Distance(g2,g7) = 304.79
    c: Coincident(g11,g4)
    c: Coincident(g11,g6)
    c: Horizontal(g11)
    c: Coincident(g12,g5)
    c: Coincident(g12,g10)
    c: Horizontal(g12)
    c: Equal(g6,g10)
    c: Equal(g10,g5)
    c: Equal(g3,g7)
    c: Equal(g7,g9)
    c: Coincident(g13,g6)
    c: Coincident(g13,g9)
    c: PointOnObject(g14,g3)
    c: PointOnObject(g14,g1)
    c: Vertical(g14)
    c: PointOnObject(g15,g7)
    c: PointOnObject(g15,g9)
    c: Vertical(g15)
    c: Distance(g14,g1) = 31.75
    c: Coincident(g16,g15)
    c: Coincident(g17,g8)
    c: Coincident(g17,g15)
    c: Coincident(g18,g14)
    c: Coincident(g18,g1)
    c: Equal(g17,g18)
    c: Distance(g6,g10) = 139.7
FEATURE [Sketcher::SketchObject] Sketch030
  ExternalGeometry = -> [Sketch029]
  FullyConstrained = true
  Placement = pos=(0,0,0) rot=(1,0,0;1.5708rad)
  sketch-geometry (4):
    g0: LineSegment StartX=-221.052 StartY=111.344 StartZ=0 EndX=-233.752 EndY=111.344 EndZ=0
    g1: LineSegment StartX=-233.752 StartY=111.344 StartZ=0 EndX=-233.752 EndY=92.2945 EndZ=0
    g2: LineSegment StartX=-233.752 StartY=92.2945 StartZ=0 EndX=-221.052 EndY=92.2945 EndZ=0
    g3: LineSegment StartX=-221.052 StartY=92.2945 StartZ=0 EndX=-221.052 EndY=111.344 EndZ=0
  constraints (12):
    c: Coincident(g0,g1)
    c: Coincident(g1,g2)
    c: Coincident(g2,g3)
    c: Coincident(g3,g0)
    c: Horizontal(g0)
    c: Horizontal(g2)
    c: Vertical(g1)
    c: Vertical(g3)
    c: Distance(g3) = 19.05
    c: Distance(g0) = 12.7
    c: PointOnObject(g0,g-3)
    c: Distance(g0,g-3) = 28.575
FEATURE [Sketcher::SketchObject] Sketch031
  ExternalGeometry = -> [Sketch028]
  FullyConstrained = true
  MapMode = 2
  Placement = pos=(0,0,0) rot=(1,0,0;1.5708rad)
  Support = -> [Sketch028]
  sketch-geometry (4):
    g0: LineSegment StartX=20.2379 StartY=111.344 StartZ=0 EndX=32.9379 EndY=111.344 EndZ=0
    g1: LineSegment StartX=32.9379 StartY=111.344 StartZ=0 EndX=32.9379 EndY=92.2945 EndZ=0
    g2: LineSegment StartX=32.9379 StartY=92.2945 StartZ=0 EndX=20.2379 EndY=92.2945 EndZ=0
    g3: LineSegment StartX=20.2379 StartY=92.2945 StartZ=0 EndX=20.2379 EndY=111.344 EndZ=0
  constraints (12):
    c: Coincident(g0,g1)
    c: Coincident(g1,g2)
    c: Coincident(g2,g3)
    c: Coincident(g3,g0)
    c: Horizontal(g0)
    c: Horizontal(g2)
    c: Vertical(g1)
    c: Vertical(g3)
    c: Distance(g1) = 19.05
    c: Distance(g0) = 12.7
    c: PointOnObject(g0,g-3)
    c: Distance(g0,g-3) = 28.575
FEATURE [Surface::Filling] Surface018
  Anisotropy = false
  BoundaryEdges = -> [Sketch028]
  BoundaryOrder = [0,0,0,0,0,0,0,0,0,0,0,0]
  Degree = 3
  Iterations = 2
  MaximumDegree = 8
  MaximumSegments = 9
  PointsOnCurve = 15
  TolAngular = 0.01
  TolCurvature = 0.1
  Tolerance2d = 1e-05
  Tolerance3d = 0.0001
FEATURE [Part::Extrusion] Extrude025
  Base = -> Surface018
  Dir = (0,19.05,0)
  DirMode = 0
  FaceMakerClass = Part::FaceMakerBullseye
  LengthFwd = 19.05
  LengthRev = 0
  Solid = true
  Symmetric = false
FEATURE [Surface::Filling] Surface019  label="hole004"
  Anisotropy = false
  BoundaryEdges = -> [Sketch031]
  BoundaryOrder = [0,0,0,0]
  Degree = 3
  Iterations = 2
  MaximumDegree = 8
  MaximumSegments = 9
  PointsOnCurve = 15
  TolAngular = 0.01
  TolCurvature = 0.1
  Tolerance2d = 1e-05
  Tolerance3d = 0.0001
FEATURE [Part::Extrusion] Extrude027
  Base = -> Surface019
  Dir = (0,100,-1)
  DirMode = 0
  FaceMakerClass = Part::FaceMakerBullseye
  LengthFwd = 100
  LengthRev = 0
  Solid = false
  Symmetric = false
FEATURE [Surface::Filling] Surface020  label="hole005"
  Anisotropy = false
  BoundaryEdges = -> [Sketch030]
  BoundaryOrder = [0,0,0,0]
  Degree = 3
  Iterations = 2
  MaximumDegree = 8
  MaximumSegments = 9
  PointsOnCurve = 15
  TolAngular = 0.01
  TolCurvature = 0.1
  Tolerance2d = 1e-05
  Tolerance3d = 0.0001
FEATURE [Part::Extrusion] Extrude026
  Base = -> Surface020
  Dir = (0,200,0)
  DirMode = 0
  FaceMakerClass = Part::FaceMakerBullseye
  LengthFwd = 100
  LengthRev = 0
  Solid = true
  Symmetric = false
FEATURE [Part::Cut] Cut006
  Base = -> Extrude025
  Tool = -> Extrude026
FEATURE [Part::Cut] Cut007
  Base = -> Cut006
  Placement = pos=(0,0,668) rot=(0,0,1;0rad)
  Tool = -> Extrude027
FEATURE [App::DocumentObjectGroup] Group001  label="work"
  Group = -> [Extrude021,Part021,Sketch025,Cut007,Sketch028,XZ_Plane026,XZ_Plane027,Sketch029,Sketch030,Sketch031,logo_Mesh]
